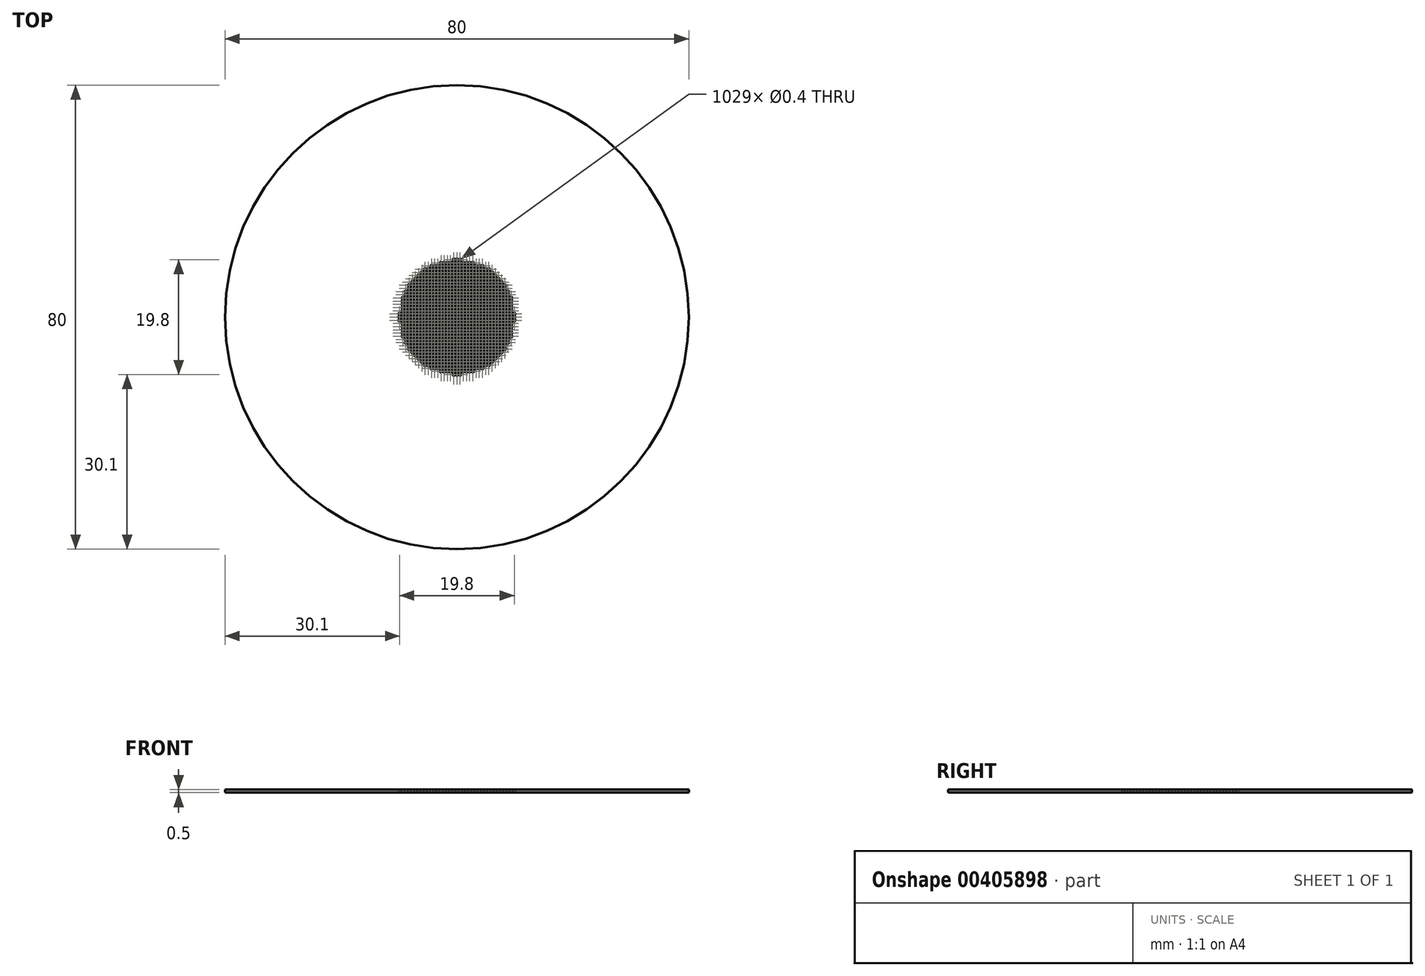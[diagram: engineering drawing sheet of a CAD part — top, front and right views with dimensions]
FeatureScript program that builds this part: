
annotation { "Feature Type Name" : "Feature", "Feature Type Description" : "" }
export const myFeature = defineFeature(function(context is Context, id is Id, definition is map)
    precondition{}
    {
        {
            var Q0;
            Q0=qCreatedBy(makeId("Top.planeOp"),FACE);
            var sketch = newSketch(context, id + "F0", { "sketchPlane" : qUnion([Q0])});
            skCircle(sketch, "E0", {"center": v(0, 0) * mm, "radius": 0.2 * mm});
            skCircle(sketch, "E1.0.1.0", {"center": v(0, 0.55) * mm, "radius": 0.2 * mm});
            skCircle(sketch, "E1.0.2.0", {"center": v(0, 1.1) * mm, "radius": 0.2 * mm});
            skCircle(sketch, "E1.0.3.0", {"center": v(0, 1.65) * mm, "radius": 0.2 * mm});
            skCircle(sketch, "E1.0.4.0", {"center": v(0, 2.2) * mm, "radius": 0.2 * mm});
            skCircle(sketch, "E1.0.5.0", {"center": v(0, 2.75) * mm, "radius": 0.2 * mm});
            skCircle(sketch, "E1.0.6.0", {"center": v(0, 3.3) * mm, "radius": 0.2 * mm});
            skCircle(sketch, "E1.0.7.0", {"center": v(0, 3.85) * mm, "radius": 0.2 * mm});
            skCircle(sketch, "E1.0.8.0", {"center": v(0, 4.4) * mm, "radius": 0.2 * mm});
            skCircle(sketch, "E1.0.9.0", {"center": v(0, 4.95) * mm, "radius": 0.2 * mm});
            skCircle(sketch, "E1.0.10.0", {"center": v(0, 5.5) * mm, "radius": 0.2 * mm});
            skCircle(sketch, "E1.0.11.0", {"center": v(0, 6.05) * mm, "radius": 0.2 * mm});
            skCircle(sketch, "E1.0.12.0", {"center": v(0, 6.6) * mm, "radius": 0.2 * mm});
            skCircle(sketch, "E1.0.13.0", {"center": v(0, 7.15) * mm, "radius": 0.2 * mm});
            skCircle(sketch, "E1.0.14.0", {"center": v(0, 7.7) * mm, "radius": 0.2 * mm});
            skCircle(sketch, "E1.0.15.0", {"center": v(0, 8.25) * mm, "radius": 0.2 * mm});
            skCircle(sketch, "E1.0.16.0", {"center": v(0, 8.8) * mm, "radius": 0.2 * mm});
            skCircle(sketch, "E1.0.17.0", {"center": v(0, 9.35) * mm, "radius": 0.2 * mm});
            skCircle(sketch, "E1.0.18.0", {"center": v(0, 9.9) * mm, "radius": 0.2 * mm});
            skCircle(sketch, "E1.1.0.0", {"center": v(0.55, 0) * mm, "radius": 0.2 * mm});
            skCircle(sketch, "E1.1.1.0", {"center": v(0.55, 0.55) * mm, "radius": 0.2 * mm});
            skCircle(sketch, "E1.1.2.0", {"center": v(0.55, 1.1) * mm, "radius": 0.2 * mm});
            skCircle(sketch, "E1.1.3.0", {"center": v(0.55, 1.65) * mm, "radius": 0.2 * mm});
            skCircle(sketch, "E1.1.4.0", {"center": v(0.55, 2.2) * mm, "radius": 0.2 * mm});
            skCircle(sketch, "E1.1.5.0", {"center": v(0.55, 2.75) * mm, "radius": 0.2 * mm});
            skCircle(sketch, "E1.1.6.0", {"center": v(0.55, 3.3) * mm, "radius": 0.2 * mm});
            skCircle(sketch, "E1.1.7.0", {"center": v(0.55, 3.85) * mm, "radius": 0.2 * mm});
            skCircle(sketch, "E1.1.8.0", {"center": v(0.55, 4.4) * mm, "radius": 0.2 * mm});
            skCircle(sketch, "E1.1.9.0", {"center": v(0.55, 4.95) * mm, "radius": 0.2 * mm});
            skCircle(sketch, "E1.1.10.0", {"center": v(0.55, 5.5) * mm, "radius": 0.2 * mm});
            skCircle(sketch, "E1.1.11.0", {"center": v(0.55, 6.05) * mm, "radius": 0.2 * mm});
            skCircle(sketch, "E1.1.12.0", {"center": v(0.55, 6.6) * mm, "radius": 0.2 * mm});
            skCircle(sketch, "E1.1.13.0", {"center": v(0.55, 7.15) * mm, "radius": 0.2 * mm});
            skCircle(sketch, "E1.1.14.0", {"center": v(0.55, 7.7) * mm, "radius": 0.2 * mm});
            skCircle(sketch, "E1.1.15.0", {"center": v(0.55, 8.25) * mm, "radius": 0.2 * mm});
            skCircle(sketch, "E1.1.16.0", {"center": v(0.55, 8.8) * mm, "radius": 0.2 * mm});
            skCircle(sketch, "E1.1.17.0", {"center": v(0.55, 9.35) * mm, "radius": 0.2 * mm});
            skCircle(sketch, "E1.1.18.0", {"center": v(0.55, 9.9) * mm, "radius": 0.2 * mm});
            skCircle(sketch, "E1.2.0.0", {"center": v(1.1, 0) * mm, "radius": 0.2 * mm});
            skCircle(sketch, "E1.2.1.0", {"center": v(1.1, 0.55) * mm, "radius": 0.2 * mm});
            skCircle(sketch, "E1.2.2.0", {"center": v(1.1, 1.1) * mm, "radius": 0.2 * mm});
            skCircle(sketch, "E1.2.3.0", {"center": v(1.1, 1.65) * mm, "radius": 0.2 * mm});
            skCircle(sketch, "E1.2.4.0", {"center": v(1.1, 2.2) * mm, "radius": 0.2 * mm});
            skCircle(sketch, "E1.2.5.0", {"center": v(1.1, 2.75) * mm, "radius": 0.2 * mm});
            skCircle(sketch, "E1.2.6.0", {"center": v(1.1, 3.3) * mm, "radius": 0.2 * mm});
            skCircle(sketch, "E1.2.7.0", {"center": v(1.1, 3.85) * mm, "radius": 0.2 * mm});
            skCircle(sketch, "E1.2.8.0", {"center": v(1.1, 4.4) * mm, "radius": 0.2 * mm});
            skCircle(sketch, "E1.2.9.0", {"center": v(1.1, 4.95) * mm, "radius": 0.2 * mm});
            skCircle(sketch, "E1.2.10.0", {"center": v(1.1, 5.5) * mm, "radius": 0.2 * mm});
            skCircle(sketch, "E1.2.11.0", {"center": v(1.1, 6.05) * mm, "radius": 0.2 * mm});
            skCircle(sketch, "E1.2.12.0", {"center": v(1.1, 6.6) * mm, "radius": 0.2 * mm});
            skCircle(sketch, "E1.2.13.0", {"center": v(1.1, 7.15) * mm, "radius": 0.2 * mm});
            skCircle(sketch, "E1.2.14.0", {"center": v(1.1, 7.7) * mm, "radius": 0.2 * mm});
            skCircle(sketch, "E1.2.15.0", {"center": v(1.1, 8.25) * mm, "radius": 0.2 * mm});
            skCircle(sketch, "E1.2.16.0", {"center": v(1.1, 8.8) * mm, "radius": 0.2 * mm});
            skCircle(sketch, "E1.2.17.0", {"center": v(1.1, 9.35) * mm, "radius": 0.2 * mm});
            skCircle(sketch, "E1.3.0.0", {"center": v(1.65, 0) * mm, "radius": 0.2 * mm});
            skCircle(sketch, "E1.3.1.0", {"center": v(1.65, 0.55) * mm, "radius": 0.2 * mm});
            skCircle(sketch, "E1.3.2.0", {"center": v(1.65, 1.1) * mm, "radius": 0.2 * mm});
            skCircle(sketch, "E1.3.3.0", {"center": v(1.65, 1.65) * mm, "radius": 0.2 * mm});
            skCircle(sketch, "E1.3.4.0", {"center": v(1.65, 2.2) * mm, "radius": 0.2 * mm});
            skCircle(sketch, "E1.3.5.0", {"center": v(1.65, 2.75) * mm, "radius": 0.2 * mm});
            skCircle(sketch, "E1.3.6.0", {"center": v(1.65, 3.3) * mm, "radius": 0.2 * mm});
            skCircle(sketch, "E1.3.7.0", {"center": v(1.65, 3.85) * mm, "radius": 0.2 * mm});
            skCircle(sketch, "E1.3.8.0", {"center": v(1.65, 4.4) * mm, "radius": 0.2 * mm});
            skCircle(sketch, "E1.3.9.0", {"center": v(1.65, 4.95) * mm, "radius": 0.2 * mm});
            skCircle(sketch, "E1.3.10.0", {"center": v(1.65, 5.5) * mm, "radius": 0.2 * mm});
            skCircle(sketch, "E1.3.11.0", {"center": v(1.65, 6.05) * mm, "radius": 0.2 * mm});
            skCircle(sketch, "E1.3.12.0", {"center": v(1.65, 6.6) * mm, "radius": 0.2 * mm});
            skCircle(sketch, "E1.3.13.0", {"center": v(1.65, 7.15) * mm, "radius": 0.2 * mm});
            skCircle(sketch, "E1.3.14.0", {"center": v(1.65, 7.7) * mm, "radius": 0.2 * mm});
            skCircle(sketch, "E1.3.15.0", {"center": v(1.65, 8.25) * mm, "radius": 0.2 * mm});
            skCircle(sketch, "E1.3.16.0", {"center": v(1.65, 8.8) * mm, "radius": 0.2 * mm});
            skCircle(sketch, "E1.3.17.0", {"center": v(1.65, 9.35) * mm, "radius": 0.2 * mm});
            skCircle(sketch, "E1.4.0.0", {"center": v(2.2, 0) * mm, "radius": 0.2 * mm});
            skCircle(sketch, "E1.4.1.0", {"center": v(2.2, 0.55) * mm, "radius": 0.2 * mm});
            skCircle(sketch, "E1.4.2.0", {"center": v(2.2, 1.1) * mm, "radius": 0.2 * mm});
            skCircle(sketch, "E1.4.3.0", {"center": v(2.2, 1.65) * mm, "radius": 0.2 * mm});
            skCircle(sketch, "E1.4.4.0", {"center": v(2.2, 2.2) * mm, "radius": 0.2 * mm});
            skCircle(sketch, "E1.4.5.0", {"center": v(2.2, 2.75) * mm, "radius": 0.2 * mm});
            skCircle(sketch, "E1.4.6.0", {"center": v(2.2, 3.3) * mm, "radius": 0.2 * mm});
            skCircle(sketch, "E1.4.7.0", {"center": v(2.2, 3.85) * mm, "radius": 0.2 * mm});
            skCircle(sketch, "E1.4.8.0", {"center": v(2.2, 4.4) * mm, "radius": 0.2 * mm});
            skCircle(sketch, "E1.4.9.0", {"center": v(2.2, 4.95) * mm, "radius": 0.2 * mm});
            skCircle(sketch, "E1.4.10.0", {"center": v(2.2, 5.5) * mm, "radius": 0.2 * mm});
            skCircle(sketch, "E1.4.11.0", {"center": v(2.2, 6.05) * mm, "radius": 0.2 * mm});
            skCircle(sketch, "E1.4.12.0", {"center": v(2.2, 6.6) * mm, "radius": 0.2 * mm});
            skCircle(sketch, "E1.4.13.0", {"center": v(2.2, 7.15) * mm, "radius": 0.2 * mm});
            skCircle(sketch, "E1.4.14.0", {"center": v(2.2, 7.7) * mm, "radius": 0.2 * mm});
            skCircle(sketch, "E1.4.15.0", {"center": v(2.2, 8.25) * mm, "radius": 0.2 * mm});
            skCircle(sketch, "E1.4.16.0", {"center": v(2.2, 8.8) * mm, "radius": 0.2 * mm});
            skCircle(sketch, "E1.4.17.0", {"center": v(2.2, 9.35) * mm, "radius": 0.2 * mm});
            skCircle(sketch, "E1.5.0.0", {"center": v(2.75, 0) * mm, "radius": 0.2 * mm});
            skCircle(sketch, "E1.5.1.0", {"center": v(2.75, 0.55) * mm, "radius": 0.2 * mm});
            skCircle(sketch, "E1.5.2.0", {"center": v(2.75, 1.1) * mm, "radius": 0.2 * mm});
            skCircle(sketch, "E1.5.3.0", {"center": v(2.75, 1.65) * mm, "radius": 0.2 * mm});
            skCircle(sketch, "E1.5.4.0", {"center": v(2.75, 2.2) * mm, "radius": 0.2 * mm});
            skCircle(sketch, "E1.5.5.0", {"center": v(2.75, 2.75) * mm, "radius": 0.2 * mm});
            skCircle(sketch, "E1.5.6.0", {"center": v(2.75, 3.3) * mm, "radius": 0.2 * mm});
            skCircle(sketch, "E1.5.7.0", {"center": v(2.75, 3.85) * mm, "radius": 0.2 * mm});
            skCircle(sketch, "E1.5.8.0", {"center": v(2.75, 4.4) * mm, "radius": 0.2 * mm});
            skCircle(sketch, "E1.5.9.0", {"center": v(2.75, 4.95) * mm, "radius": 0.2 * mm});
            skCircle(sketch, "E1.5.10.0", {"center": v(2.75, 5.5) * mm, "radius": 0.2 * mm});
            skCircle(sketch, "E1.5.11.0", {"center": v(2.75, 6.05) * mm, "radius": 0.2 * mm});
            skCircle(sketch, "E1.5.12.0", {"center": v(2.75, 6.6) * mm, "radius": 0.2 * mm});
            skCircle(sketch, "E1.5.13.0", {"center": v(2.75, 7.15) * mm, "radius": 0.2 * mm});
            skCircle(sketch, "E1.5.14.0", {"center": v(2.75, 7.7) * mm, "radius": 0.2 * mm});
            skCircle(sketch, "E1.5.15.0", {"center": v(2.75, 8.25) * mm, "radius": 0.2 * mm});
            skCircle(sketch, "E1.5.16.0", {"center": v(2.75, 8.8) * mm, "radius": 0.2 * mm});
            skCircle(sketch, "E1.5.17.0", {"center": v(2.75, 9.35) * mm, "radius": 0.2 * mm});
            skCircle(sketch, "E1.6.0.0", {"center": v(3.3, 0) * mm, "radius": 0.2 * mm});
            skCircle(sketch, "E1.6.1.0", {"center": v(3.3, 0.55) * mm, "radius": 0.2 * mm});
            skCircle(sketch, "E1.6.2.0", {"center": v(3.3, 1.1) * mm, "radius": 0.2 * mm});
            skCircle(sketch, "E1.6.3.0", {"center": v(3.3, 1.65) * mm, "radius": 0.2 * mm});
            skCircle(sketch, "E1.6.4.0", {"center": v(3.3, 2.2) * mm, "radius": 0.2 * mm});
            skCircle(sketch, "E1.6.5.0", {"center": v(3.3, 2.75) * mm, "radius": 0.2 * mm});
            skCircle(sketch, "E1.6.6.0", {"center": v(3.3, 3.3) * mm, "radius": 0.2 * mm});
            skCircle(sketch, "E1.6.7.0", {"center": v(3.3, 3.85) * mm, "radius": 0.2 * mm});
            skCircle(sketch, "E1.6.8.0", {"center": v(3.3, 4.4) * mm, "radius": 0.2 * mm});
            skCircle(sketch, "E1.6.9.0", {"center": v(3.3, 4.95) * mm, "radius": 0.2 * mm});
            skCircle(sketch, "E1.6.10.0", {"center": v(3.3, 5.5) * mm, "radius": 0.2 * mm});
            skCircle(sketch, "E1.6.11.0", {"center": v(3.3, 6.05) * mm, "radius": 0.2 * mm});
            skCircle(sketch, "E1.6.12.0", {"center": v(3.3, 6.6) * mm, "radius": 0.2 * mm});
            skCircle(sketch, "E1.6.13.0", {"center": v(3.3, 7.15) * mm, "radius": 0.2 * mm});
            skCircle(sketch, "E1.6.14.0", {"center": v(3.3, 7.7) * mm, "radius": 0.2 * mm});
            skCircle(sketch, "E1.6.15.0", {"center": v(3.3, 8.25) * mm, "radius": 0.2 * mm});
            skCircle(sketch, "E1.6.16.0", {"center": v(3.3, 8.8) * mm, "radius": 0.2 * mm});
            skCircle(sketch, "E1.7.0.0", {"center": v(3.85, 0) * mm, "radius": 0.2 * mm});
            skCircle(sketch, "E1.7.1.0", {"center": v(3.85, 0.55) * mm, "radius": 0.2 * mm});
            skCircle(sketch, "E1.7.2.0", {"center": v(3.85, 1.1) * mm, "radius": 0.2 * mm});
            skCircle(sketch, "E1.7.3.0", {"center": v(3.85, 1.65) * mm, "radius": 0.2 * mm});
            skCircle(sketch, "E1.7.4.0", {"center": v(3.85, 2.2) * mm, "radius": 0.2 * mm});
            skCircle(sketch, "E1.7.5.0", {"center": v(3.85, 2.75) * mm, "radius": 0.2 * mm});
            skCircle(sketch, "E1.7.6.0", {"center": v(3.85, 3.3) * mm, "radius": 0.2 * mm});
            skCircle(sketch, "E1.7.7.0", {"center": v(3.85, 3.85) * mm, "radius": 0.2 * mm});
            skCircle(sketch, "E1.7.8.0", {"center": v(3.85, 4.4) * mm, "radius": 0.2 * mm});
            skCircle(sketch, "E1.7.9.0", {"center": v(3.85, 4.95) * mm, "radius": 0.2 * mm});
            skCircle(sketch, "E1.7.10.0", {"center": v(3.85, 5.5) * mm, "radius": 0.2 * mm});
            skCircle(sketch, "E1.7.11.0", {"center": v(3.85, 6.05) * mm, "radius": 0.2 * mm});
            skCircle(sketch, "E1.7.12.0", {"center": v(3.85, 6.6) * mm, "radius": 0.2 * mm});
            skCircle(sketch, "E1.7.13.0", {"center": v(3.85, 7.15) * mm, "radius": 0.2 * mm});
            skCircle(sketch, "E1.7.14.0", {"center": v(3.85, 7.7) * mm, "radius": 0.2 * mm});
            skCircle(sketch, "E1.7.15.0", {"center": v(3.85, 8.25) * mm, "radius": 0.2 * mm});
            skCircle(sketch, "E1.7.16.0", {"center": v(3.85, 8.8) * mm, "radius": 0.2 * mm});
            skCircle(sketch, "E1.8.0.0", {"center": v(4.4, 0) * mm, "radius": 0.2 * mm});
            skCircle(sketch, "E1.8.1.0", {"center": v(4.4, 0.55) * mm, "radius": 0.2 * mm});
            skCircle(sketch, "E1.8.2.0", {"center": v(4.4, 1.1) * mm, "radius": 0.2 * mm});
            skCircle(sketch, "E1.8.3.0", {"center": v(4.4, 1.65) * mm, "radius": 0.2 * mm});
            skCircle(sketch, "E1.8.4.0", {"center": v(4.4, 2.2) * mm, "radius": 0.2 * mm});
            skCircle(sketch, "E1.8.5.0", {"center": v(4.4, 2.75) * mm, "radius": 0.2 * mm});
            skCircle(sketch, "E1.8.6.0", {"center": v(4.4, 3.3) * mm, "radius": 0.2 * mm});
            skCircle(sketch, "E1.8.7.0", {"center": v(4.4, 3.85) * mm, "radius": 0.2 * mm});
            skCircle(sketch, "E1.8.8.0", {"center": v(4.4, 4.4) * mm, "radius": 0.2 * mm});
            skCircle(sketch, "E1.8.9.0", {"center": v(4.4, 4.95) * mm, "radius": 0.2 * mm});
            skCircle(sketch, "E1.8.10.0", {"center": v(4.4, 5.5) * mm, "radius": 0.2 * mm});
            skCircle(sketch, "E1.8.11.0", {"center": v(4.4, 6.05) * mm, "radius": 0.2 * mm});
            skCircle(sketch, "E1.8.12.0", {"center": v(4.4, 6.6) * mm, "radius": 0.2 * mm});
            skCircle(sketch, "E1.8.13.0", {"center": v(4.4, 7.15) * mm, "radius": 0.2 * mm});
            skCircle(sketch, "E1.8.14.0", {"center": v(4.4, 7.7) * mm, "radius": 0.2 * mm});
            skCircle(sketch, "E1.8.15.0", {"center": v(4.4, 8.25) * mm, "radius": 0.2 * mm});
            skCircle(sketch, "E1.8.16.0", {"center": v(4.4, 8.8) * mm, "radius": 0.2 * mm});
            skCircle(sketch, "E1.9.0.0", {"center": v(4.95, 0) * mm, "radius": 0.2 * mm});
            skCircle(sketch, "E1.9.1.0", {"center": v(4.95, 0.55) * mm, "radius": 0.2 * mm});
            skCircle(sketch, "E1.9.2.0", {"center": v(4.95, 1.1) * mm, "radius": 0.2 * mm});
            skCircle(sketch, "E1.9.3.0", {"center": v(4.95, 1.65) * mm, "radius": 0.2 * mm});
            skCircle(sketch, "E1.9.4.0", {"center": v(4.95, 2.2) * mm, "radius": 0.2 * mm});
            skCircle(sketch, "E1.9.5.0", {"center": v(4.95, 2.75) * mm, "radius": 0.2 * mm});
            skCircle(sketch, "E1.9.6.0", {"center": v(4.95, 3.3) * mm, "radius": 0.2 * mm});
            skCircle(sketch, "E1.9.7.0", {"center": v(4.95, 3.85) * mm, "radius": 0.2 * mm});
            skCircle(sketch, "E1.9.8.0", {"center": v(4.95, 4.4) * mm, "radius": 0.2 * mm});
            skCircle(sketch, "E1.9.9.0", {"center": v(4.95, 4.95) * mm, "radius": 0.2 * mm});
            skCircle(sketch, "E1.9.10.0", {"center": v(4.95, 5.5) * mm, "radius": 0.2 * mm});
            skCircle(sketch, "E1.9.11.0", {"center": v(4.95, 6.05) * mm, "radius": 0.2 * mm});
            skCircle(sketch, "E1.9.12.0", {"center": v(4.95, 6.6) * mm, "radius": 0.2 * mm});
            skCircle(sketch, "E1.9.13.0", {"center": v(4.95, 7.15) * mm, "radius": 0.2 * mm});
            skCircle(sketch, "E1.9.14.0", {"center": v(4.95, 7.7) * mm, "radius": 0.2 * mm});
            skCircle(sketch, "E1.9.15.0", {"center": v(4.95, 8.25) * mm, "radius": 0.2 * mm});
            skCircle(sketch, "E1.10.0.0", {"center": v(5.5, 0) * mm, "radius": 0.2 * mm});
            skCircle(sketch, "E1.10.1.0", {"center": v(5.5, 0.55) * mm, "radius": 0.2 * mm});
            skCircle(sketch, "E1.10.2.0", {"center": v(5.5, 1.1) * mm, "radius": 0.2 * mm});
            skCircle(sketch, "E1.10.3.0", {"center": v(5.5, 1.65) * mm, "radius": 0.2 * mm});
            skCircle(sketch, "E1.10.4.0", {"center": v(5.5, 2.2) * mm, "radius": 0.2 * mm});
            skCircle(sketch, "E1.10.5.0", {"center": v(5.5, 2.75) * mm, "radius": 0.2 * mm});
            skCircle(sketch, "E1.10.6.0", {"center": v(5.5, 3.3) * mm, "radius": 0.2 * mm});
            skCircle(sketch, "E1.10.7.0", {"center": v(5.5, 3.85) * mm, "radius": 0.2 * mm});
            skCircle(sketch, "E1.10.8.0", {"center": v(5.5, 4.4) * mm, "radius": 0.2 * mm});
            skCircle(sketch, "E1.10.9.0", {"center": v(5.5, 4.95) * mm, "radius": 0.2 * mm});
            skCircle(sketch, "E1.10.10.0", {"center": v(5.5, 5.5) * mm, "radius": 0.2 * mm});
            skCircle(sketch, "E1.10.11.0", {"center": v(5.5, 6.05) * mm, "radius": 0.2 * mm});
            skCircle(sketch, "E1.10.12.0", {"center": v(5.5, 6.6) * mm, "radius": 0.2 * mm});
            skCircle(sketch, "E1.10.13.0", {"center": v(5.5, 7.15) * mm, "radius": 0.2 * mm});
            skCircle(sketch, "E1.10.14.0", {"center": v(5.5, 7.7) * mm, "radius": 0.2 * mm});
            skCircle(sketch, "E1.10.15.0", {"center": v(5.5, 8.25) * mm, "radius": 0.2 * mm});
            skCircle(sketch, "E1.11.0.0", {"center": v(6.05, 0) * mm, "radius": 0.2 * mm});
            skCircle(sketch, "E1.11.1.0", {"center": v(6.05, 0.55) * mm, "radius": 0.2 * mm});
            skCircle(sketch, "E1.11.2.0", {"center": v(6.05, 1.1) * mm, "radius": 0.2 * mm});
            skCircle(sketch, "E1.11.3.0", {"center": v(6.05, 1.65) * mm, "radius": 0.2 * mm});
            skCircle(sketch, "E1.11.4.0", {"center": v(6.05, 2.2) * mm, "radius": 0.2 * mm});
            skCircle(sketch, "E1.11.5.0", {"center": v(6.05, 2.75) * mm, "radius": 0.2 * mm});
            skCircle(sketch, "E1.11.6.0", {"center": v(6.05, 3.3) * mm, "radius": 0.2 * mm});
            skCircle(sketch, "E1.11.7.0", {"center": v(6.05, 3.85) * mm, "radius": 0.2 * mm});
            skCircle(sketch, "E1.11.8.0", {"center": v(6.05, 4.4) * mm, "radius": 0.2 * mm});
            skCircle(sketch, "E1.11.9.0", {"center": v(6.05, 4.95) * mm, "radius": 0.2 * mm});
            skCircle(sketch, "E1.11.10.0", {"center": v(6.05, 5.5) * mm, "radius": 0.2 * mm});
            skCircle(sketch, "E1.11.11.0", {"center": v(6.05, 6.05) * mm, "radius": 0.2 * mm});
            skCircle(sketch, "E1.11.12.0", {"center": v(6.05, 6.6) * mm, "radius": 0.2 * mm});
            skCircle(sketch, "E1.11.13.0", {"center": v(6.05, 7.15) * mm, "radius": 0.2 * mm});
            skCircle(sketch, "E1.11.14.0", {"center": v(6.05, 7.7) * mm, "radius": 0.2 * mm});
            skCircle(sketch, "E1.12.0.0", {"center": v(6.6, 0) * mm, "radius": 0.2 * mm});
            skCircle(sketch, "E1.12.1.0", {"center": v(6.6, 0.55) * mm, "radius": 0.2 * mm});
            skCircle(sketch, "E1.12.2.0", {"center": v(6.6, 1.1) * mm, "radius": 0.2 * mm});
            skCircle(sketch, "E1.12.3.0", {"center": v(6.6, 1.65) * mm, "radius": 0.2 * mm});
            skCircle(sketch, "E1.12.4.0", {"center": v(6.6, 2.2) * mm, "radius": 0.2 * mm});
            skCircle(sketch, "E1.12.5.0", {"center": v(6.6, 2.75) * mm, "radius": 0.2 * mm});
            skCircle(sketch, "E1.12.6.0", {"center": v(6.6, 3.3) * mm, "radius": 0.2 * mm});
            skCircle(sketch, "E1.12.7.0", {"center": v(6.6, 3.85) * mm, "radius": 0.2 * mm});
            skCircle(sketch, "E1.12.8.0", {"center": v(6.6, 4.4) * mm, "radius": 0.2 * mm});
            skCircle(sketch, "E1.12.9.0", {"center": v(6.6, 4.95) * mm, "radius": 0.2 * mm});
            skCircle(sketch, "E1.12.10.0", {"center": v(6.6, 5.5) * mm, "radius": 0.2 * mm});
            skCircle(sketch, "E1.12.11.0", {"center": v(6.6, 6.05) * mm, "radius": 0.2 * mm});
            skCircle(sketch, "E1.12.12.0", {"center": v(6.6, 6.6) * mm, "radius": 0.2 * mm});
            skCircle(sketch, "E1.12.13.0", {"center": v(6.6, 7.15) * mm, "radius": 0.2 * mm});
            skCircle(sketch, "E1.13.0.0", {"center": v(7.15, 0) * mm, "radius": 0.2 * mm});
            skCircle(sketch, "E1.13.1.0", {"center": v(7.15, 0.55) * mm, "radius": 0.2 * mm});
            skCircle(sketch, "E1.13.2.0", {"center": v(7.15, 1.1) * mm, "radius": 0.2 * mm});
            skCircle(sketch, "E1.13.3.0", {"center": v(7.15, 1.65) * mm, "radius": 0.2 * mm});
            skCircle(sketch, "E1.13.4.0", {"center": v(7.15, 2.2) * mm, "radius": 0.2 * mm});
            skCircle(sketch, "E1.13.5.0", {"center": v(7.15, 2.75) * mm, "radius": 0.2 * mm});
            skCircle(sketch, "E1.13.6.0", {"center": v(7.15, 3.3) * mm, "radius": 0.2 * mm});
            skCircle(sketch, "E1.13.7.0", {"center": v(7.15, 3.85) * mm, "radius": 0.2 * mm});
            skCircle(sketch, "E1.13.8.0", {"center": v(7.15, 4.4) * mm, "radius": 0.2 * mm});
            skCircle(sketch, "E1.13.9.0", {"center": v(7.15, 4.95) * mm, "radius": 0.2 * mm});
            skCircle(sketch, "E1.13.10.0", {"center": v(7.15, 5.5) * mm, "radius": 0.2 * mm});
            skCircle(sketch, "E1.13.11.0", {"center": v(7.15, 6.05) * mm, "radius": 0.2 * mm});
            skCircle(sketch, "E1.13.12.0", {"center": v(7.15, 6.6) * mm, "radius": 0.2 * mm});
            skCircle(sketch, "E1.14.0.0", {"center": v(7.7, 0) * mm, "radius": 0.2 * mm});
            skCircle(sketch, "E1.14.1.0", {"center": v(7.7, 0.55) * mm, "radius": 0.2 * mm});
            skCircle(sketch, "E1.14.2.0", {"center": v(7.7, 1.1) * mm, "radius": 0.2 * mm});
            skCircle(sketch, "E1.14.3.0", {"center": v(7.7, 1.65) * mm, "radius": 0.2 * mm});
            skCircle(sketch, "E1.14.4.0", {"center": v(7.7, 2.2) * mm, "radius": 0.2 * mm});
            skCircle(sketch, "E1.14.5.0", {"center": v(7.7, 2.75) * mm, "radius": 0.2 * mm});
            skCircle(sketch, "E1.14.6.0", {"center": v(7.7, 3.3) * mm, "radius": 0.2 * mm});
            skCircle(sketch, "E1.14.7.0", {"center": v(7.7, 3.85) * mm, "radius": 0.2 * mm});
            skCircle(sketch, "E1.14.8.0", {"center": v(7.7, 4.4) * mm, "radius": 0.2 * mm});
            skCircle(sketch, "E1.14.9.0", {"center": v(7.7, 4.95) * mm, "radius": 0.2 * mm});
            skCircle(sketch, "E1.14.10.0", {"center": v(7.7, 5.5) * mm, "radius": 0.2 * mm});
            skCircle(sketch, "E1.14.11.0", {"center": v(7.7, 6.05) * mm, "radius": 0.2 * mm});
            skCircle(sketch, "E1.15.0.0", {"center": v(8.25, 0) * mm, "radius": 0.2 * mm});
            skCircle(sketch, "E1.15.1.0", {"center": v(8.25, 0.55) * mm, "radius": 0.2 * mm});
            skCircle(sketch, "E1.15.2.0", {"center": v(8.25, 1.1) * mm, "radius": 0.2 * mm});
            skCircle(sketch, "E1.15.3.0", {"center": v(8.25, 1.65) * mm, "radius": 0.2 * mm});
            skCircle(sketch, "E1.15.4.0", {"center": v(8.25, 2.2) * mm, "radius": 0.2 * mm});
            skCircle(sketch, "E1.15.5.0", {"center": v(8.25, 2.75) * mm, "radius": 0.2 * mm});
            skCircle(sketch, "E1.15.6.0", {"center": v(8.25, 3.3) * mm, "radius": 0.2 * mm});
            skCircle(sketch, "E1.15.7.0", {"center": v(8.25, 3.85) * mm, "radius": 0.2 * mm});
            skCircle(sketch, "E1.15.8.0", {"center": v(8.25, 4.4) * mm, "radius": 0.2 * mm});
            skCircle(sketch, "E1.15.9.0", {"center": v(8.25, 4.95) * mm, "radius": 0.2 * mm});
            skCircle(sketch, "E1.15.10.0", {"center": v(8.25, 5.5) * mm, "radius": 0.2 * mm});
            skCircle(sketch, "E1.16.0.0", {"center": v(8.8, 0) * mm, "radius": 0.2 * mm});
            skCircle(sketch, "E1.16.1.0", {"center": v(8.8, 0.55) * mm, "radius": 0.2 * mm});
            skCircle(sketch, "E1.16.2.0", {"center": v(8.8, 1.1) * mm, "radius": 0.2 * mm});
            skCircle(sketch, "E1.16.3.0", {"center": v(8.8, 1.65) * mm, "radius": 0.2 * mm});
            skCircle(sketch, "E1.16.4.0", {"center": v(8.8, 2.2) * mm, "radius": 0.2 * mm});
            skCircle(sketch, "E1.16.5.0", {"center": v(8.8, 2.75) * mm, "radius": 0.2 * mm});
            skCircle(sketch, "E1.16.6.0", {"center": v(8.8, 3.3) * mm, "radius": 0.2 * mm});
            skCircle(sketch, "E1.16.7.0", {"center": v(8.8, 3.85) * mm, "radius": 0.2 * mm});
            skCircle(sketch, "E1.16.8.0", {"center": v(8.8, 4.4) * mm, "radius": 0.2 * mm});
            skCircle(sketch, "E1.17.0.0", {"center": v(9.35, 0) * mm, "radius": 0.2 * mm});
            skCircle(sketch, "E1.17.1.0", {"center": v(9.35, 0.55) * mm, "radius": 0.2 * mm});
            skCircle(sketch, "E1.17.2.0", {"center": v(9.35, 1.1) * mm, "radius": 0.2 * mm});
            skCircle(sketch, "E1.17.3.0", {"center": v(9.35, 1.65) * mm, "radius": 0.2 * mm});
            skCircle(sketch, "E1.17.4.0", {"center": v(9.35, 2.2) * mm, "radius": 0.2 * mm});
            skCircle(sketch, "E1.17.5.0", {"center": v(9.35, 2.75) * mm, "radius": 0.2 * mm});
            skCircle(sketch, "E1.17.6.0", {"center": v(9.35, 3.3) * mm, "radius": 0.2 * mm});
            skCircle(sketch, "E1.18.0.0", {"center": v(9.9, 0) * mm, "radius": 0.2 * mm});
            skCircle(sketch, "E1.18.1.0", {"center": v(9.9, 0.55) * mm, "radius": 0.2 * mm});
            skLineSegment(sketch, "E1.direction1", {"start": v(0, 0) * mm, "end": v(0.55, 0) * mm, "construction": true});
            skLineSegment(sketch, "E1.direction2", {"start": v(0, 0) * mm, "end": v(0, 0.55) * mm, "construction": true});
            skCircle(sketch, "E2.MirrorC", {"center": v(3.3, -1.1) * mm, "radius": 0.2 * mm});
            skCircle(sketch, "E3.MirrorC", {"center": v(2.75, -2.2) * mm, "radius": 0.2 * mm});
            skCircle(sketch, "E4.MirrorC", {"center": v(5.5, -8.25) * mm, "radius": 0.2 * mm});
            skCircle(sketch, "E5.MirrorC", {"center": v(4.95, -8.25) * mm, "radius": 0.2 * mm});
            skCircle(sketch, "E6.MirrorC", {"center": v(4.4, -8.8) * mm, "radius": 0.2 * mm});
            skCircle(sketch, "E7.MirrorC", {"center": v(9.35, -2.75) * mm, "radius": 0.2 * mm});
            skCircle(sketch, "E8.MirrorC", {"center": v(8.25, -4.95) * mm, "radius": 0.2 * mm});
            skCircle(sketch, "E9.MirrorC", {"center": v(7.15, -1.1) * mm, "radius": 0.2 * mm});
            skCircle(sketch, "E10.MirrorC", {"center": v(7.7, -2.75) * mm, "radius": 0.2 * mm});
            skCircle(sketch, "E11.MirrorC", {"center": v(4.4, -2.75) * mm, "radius": 0.2 * mm});
            skCircle(sketch, "E12.MirrorC", {"center": v(2.2, -3.3) * mm, "radius": 0.2 * mm});
            skCircle(sketch, "E13.MirrorC", {"center": v(1.65, -4.4) * mm, "radius": 0.2 * mm});
            skCircle(sketch, "E14.MirrorC", {"center": v(1.1, -5.5) * mm, "radius": 0.2 * mm});
            skCircle(sketch, "E15.MirrorC", {"center": v(2.2, -2.75) * mm, "radius": 0.2 * mm});
            skCircle(sketch, "E16.MirrorC", {"center": v(1.65, -3.85) * mm, "radius": 0.2 * mm});
            skCircle(sketch, "E17.MirrorC", {"center": v(1.1, -4.95) * mm, "radius": 0.2 * mm});
            skCircle(sketch, "E18.MirrorC", {"center": v(3.85, -8.8) * mm, "radius": 0.2 * mm});
            skCircle(sketch, "E19.MirrorC", {"center": v(2.75, -1.65) * mm, "radius": 0.2 * mm});
            skCircle(sketch, "E20.MirrorC", {"center": v(6.05, -7.7) * mm, "radius": 0.2 * mm});
            skCircle(sketch, "E21.MirrorC", {"center": v(5.5, -7.7) * mm, "radius": 0.2 * mm});
            skCircle(sketch, "E22.MirrorC", {"center": v(4.95, -7.7) * mm, "radius": 0.2 * mm});
            skCircle(sketch, "E23.MirrorC", {"center": v(4.4, -8.25) * mm, "radius": 0.2 * mm});
            skCircle(sketch, "E24.MirrorC", {"center": v(9.35, -2.2) * mm, "radius": 0.2 * mm});
            skCircle(sketch, "E25.MirrorC", {"center": v(8.25, -4.4) * mm, "radius": 0.2 * mm});
            skCircle(sketch, "E26.MirrorC", {"center": v(3.3, -3.85) * mm, "radius": 0.2 * mm});
            skCircle(sketch, "E27.MirrorC", {"center": v(7.7, -2.2) * mm, "radius": 0.2 * mm});
            skCircle(sketch, "E28.MirrorC", {"center": v(3.85, -3.3) * mm, "radius": 0.2 * mm});
            skCircle(sketch, "E29.MirrorC", {"center": v(2.75, -4.95) * mm, "radius": 0.2 * mm});
            skCircle(sketch, "E30.MirrorC", {"center": v(6.6, -2.75) * mm, "radius": 0.2 * mm});
            skCircle(sketch, "E31.MirrorC", {"center": v(5.5, -2.2) * mm, "radius": 0.2 * mm});
            skCircle(sketch, "E32.MirrorC", {"center": v(6.05, -2.2) * mm, "radius": 0.2 * mm});
            skCircle(sketch, "E33.MirrorC", {"center": v(4.95, -2.2) * mm, "radius": 0.2 * mm});
            skCircle(sketch, "E34.MirrorC", {"center": v(8.8, -1.65) * mm, "radius": 0.2 * mm});
            skCircle(sketch, "E35.MirrorC", {"center": v(7.7, -5.5) * mm, "radius": 0.2 * mm});
            skCircle(sketch, "E36.MirrorC", {"center": v(7.15, -3.85) * mm, "radius": 0.2 * mm});
            skCircle(sketch, "E37.MirrorC", {"center": v(8.25, -5.5) * mm, "radius": 0.2 * mm});
            skCircle(sketch, "E38.MirrorC", {"center": v(9.35, -3.3) * mm, "radius": 0.2 * mm});
            skCircle(sketch, "E39.MirrorC", {"center": v(7.7, -3.3) * mm, "radius": 0.2 * mm});
            skCircle(sketch, "E40.MirrorC", {"center": v(7.15, -1.65) * mm, "radius": 0.2 * mm});
            skCircle(sketch, "E41.MirrorC", {"center": v(1.65, -4.95) * mm, "radius": 0.2 * mm});
            skCircle(sketch, "E42.MirrorC", {"center": v(2.2, -3.85) * mm, "radius": 0.2 * mm});
            skCircle(sketch, "E43.MirrorC", {"center": v(1.1, -6.05) * mm, "radius": 0.2 * mm});
            skCircle(sketch, "E44.MirrorC", {"center": v(3.85, -1.1) * mm, "radius": 0.2 * mm});
            skCircle(sketch, "E45.MirrorC", {"center": v(2.75, -2.75) * mm, "radius": 0.2 * mm});
            skCircle(sketch, "E46.MirrorC", {"center": v(3.3, -1.65) * mm, "radius": 0.2 * mm});
            skCircle(sketch, "E47.MirrorC", {"center": v(1.65, -7.7) * mm, "radius": 0.2 * mm});
            skCircle(sketch, "E48.MirrorC", {"center": v(2.2, -6.6) * mm, "radius": 0.2 * mm});
            skCircle(sketch, "E49.MirrorC", {"center": v(4.4, -3.3) * mm, "radius": 0.2 * mm});
            skCircle(sketch, "E50.MirrorC", {"center": v(1.1, -8.8) * mm, "radius": 0.2 * mm});
            skCircle(sketch, "E51.MirrorC", {"center": v(3.85, -3.85) * mm, "radius": 0.2 * mm});
            skCircle(sketch, "E52.MirrorC", {"center": v(3.3, -4.4) * mm, "radius": 0.2 * mm});
            skCircle(sketch, "E53.MirrorC", {"center": v(2.75, -5.5) * mm, "radius": 0.2 * mm});
            skCircle(sketch, "E54.MirrorC", {"center": v(6.6, -3.3) * mm, "radius": 0.2 * mm});
            skCircle(sketch, "E55.MirrorC", {"center": v(6.05, -2.75) * mm, "radius": 0.2 * mm});
            skCircle(sketch, "E56.MirrorC", {"center": v(5.5, -2.75) * mm, "radius": 0.2 * mm});
            skCircle(sketch, "E57.MirrorC", {"center": v(4.95, -2.75) * mm, "radius": 0.2 * mm});
            skCircle(sketch, "E58.MirrorC", {"center": v(8.8, -2.2) * mm, "radius": 0.2 * mm});
            skCircle(sketch, "E59.MirrorC", {"center": v(7.7, -6.05) * mm, "radius": 0.2 * mm});
            skCircle(sketch, "E60.MirrorC", {"center": v(7.15, -4.4) * mm, "radius": 0.2 * mm});
            skCircle(sketch, "E61.MirrorC", {"center": v(1.1, -9.35) * mm, "radius": 0.2 * mm});
            skCircle(sketch, "E62.MirrorC", {"center": v(3.3, -4.95) * mm, "radius": 0.2 * mm});
            skCircle(sketch, "E63.MirrorC", {"center": v(2.75, -6.05) * mm, "radius": 0.2 * mm});
            skCircle(sketch, "E64.MirrorC", {"center": v(2.2, -7.15) * mm, "radius": 0.2 * mm});
            skCircle(sketch, "E65.MirrorC", {"center": v(1.65, -8.25) * mm, "radius": 0.2 * mm});
            skCircle(sketch, "E66.MirrorC", {"center": v(5.5, -3.3) * mm, "radius": 0.2 * mm});
            skCircle(sketch, "E67.MirrorC", {"center": v(3.85, -4.4) * mm, "radius": 0.2 * mm});
            skCircle(sketch, "E68.MirrorC", {"center": v(4.95, -3.3) * mm, "radius": 0.2 * mm});
            skCircle(sketch, "E69.MirrorC", {"center": v(7.15, -4.95) * mm, "radius": 0.2 * mm});
            skCircle(sketch, "E70.MirrorC", {"center": v(4.4, -3.85) * mm, "radius": 0.2 * mm});
            skCircle(sketch, "E71.MirrorC", {"center": v(6.05, -3.3) * mm, "radius": 0.2 * mm});
            skCircle(sketch, "E72.MirrorC", {"center": v(6.6, -3.85) * mm, "radius": 0.2 * mm});
            skCircle(sketch, "E73.MirrorC", {"center": v(8.8, -2.75) * mm, "radius": 0.2 * mm});
            skCircle(sketch, "E74.MirrorC", {"center": v(1.1, -1.1) * mm, "radius": 0.2 * mm});
            skCircle(sketch, "E75.MirrorC", {"center": v(3.3, -5.5) * mm, "radius": 0.2 * mm});
            skCircle(sketch, "E76.MirrorC", {"center": v(2.75, -6.6) * mm, "radius": 0.2 * mm});
            skCircle(sketch, "E77.MirrorC", {"center": v(2.2, -7.7) * mm, "radius": 0.2 * mm});
            skCircle(sketch, "E78.MirrorC", {"center": v(1.65, -8.8) * mm, "radius": 0.2 * mm});
            skCircle(sketch, "E79.MirrorC", {"center": v(5.5, -3.85) * mm, "radius": 0.2 * mm});
            skCircle(sketch, "E80.MirrorC", {"center": v(4.95, -3.85) * mm, "radius": 0.2 * mm});
            skCircle(sketch, "E81.MirrorC", {"center": v(4.4, -4.4) * mm, "radius": 0.2 * mm});
            skCircle(sketch, "E82.MirrorC", {"center": v(3.85, -4.95) * mm, "radius": 0.2 * mm});
            skCircle(sketch, "E83.MirrorC", {"center": v(6.05, -4.4) * mm, "radius": 0.2 * mm});
            skCircle(sketch, "E84.MirrorC", {"center": v(6.6, -4.95) * mm, "radius": 0.2 * mm});
            skCircle(sketch, "E85.MirrorC", {"center": v(7.15, -6.05) * mm, "radius": 0.2 * mm});
            skCircle(sketch, "E86.MirrorC", {"center": v(8.25, -1.1) * mm, "radius": 0.2 * mm});
            skCircle(sketch, "E87.MirrorC", {"center": v(3.85, -5.5) * mm, "radius": 0.2 * mm});
            skCircle(sketch, "E88.MirrorC", {"center": v(4.4, -4.95) * mm, "radius": 0.2 * mm});
            skCircle(sketch, "E89.MirrorC", {"center": v(5.5, -4.4) * mm, "radius": 0.2 * mm});
            skCircle(sketch, "E90.MirrorC", {"center": v(4.95, -4.4) * mm, "radius": 0.2 * mm});
            skCircle(sketch, "E91.MirrorC", {"center": v(1.65, -9.35) * mm, "radius": 0.2 * mm});
            skCircle(sketch, "E92.MirrorC", {"center": v(2.2, -8.25) * mm, "radius": 0.2 * mm});
            skCircle(sketch, "E93.MirrorC", {"center": v(3.3, -6.05) * mm, "radius": 0.2 * mm});
            skCircle(sketch, "E94.MirrorC", {"center": v(2.75, -7.15) * mm, "radius": 0.2 * mm});
            skCircle(sketch, "E95.MirrorC", {"center": v(1.1, -8.25) * mm, "radius": 0.2 * mm});
            skCircle(sketch, "E96.MirrorC", {"center": v(1.65, -7.15) * mm, "radius": 0.2 * mm});
            skCircle(sketch, "E97.MirrorC", {"center": v(2.2, -6.05) * mm, "radius": 0.2 * mm});
            skCircle(sketch, "E98.MirrorC", {"center": v(7.7, -4.95) * mm, "radius": 0.2 * mm});
            skCircle(sketch, "E99.MirrorC", {"center": v(7.15, -3.3) * mm, "radius": 0.2 * mm});
            skCircle(sketch, "E100.MirrorC", {"center": v(8.8, -1.1) * mm, "radius": 0.2 * mm});
            skCircle(sketch, "E101.MirrorC", {"center": v(4.95, -1.65) * mm, "radius": 0.2 * mm});
            skCircle(sketch, "E102.MirrorC", {"center": v(5.5, -1.65) * mm, "radius": 0.2 * mm});
            skCircle(sketch, "E103.MirrorC", {"center": v(6.05, -1.65) * mm, "radius": 0.2 * mm});
            skCircle(sketch, "E104.MirrorC", {"center": v(6.6, -2.2) * mm, "radius": 0.2 * mm});
            skCircle(sketch, "E105.MirrorC", {"center": v(2.75, -4.4) * mm, "radius": 0.2 * mm});
            skCircle(sketch, "E106.MirrorC", {"center": v(3.85, -2.75) * mm, "radius": 0.2 * mm});
            skCircle(sketch, "E107.MirrorC", {"center": v(3.3, -3.3) * mm, "radius": 0.2 * mm});
            skCircle(sketch, "E108.MirrorC", {"center": v(4.4, -2.2) * mm, "radius": 0.2 * mm});
            skCircle(sketch, "E109.MirrorC", {"center": v(1.1, -7.7) * mm, "radius": 0.2 * mm});
            skCircle(sketch, "E110.MirrorC", {"center": v(1.65, -6.6) * mm, "radius": 0.2 * mm});
            skCircle(sketch, "E111.MirrorC", {"center": v(2.2, -5.5) * mm, "radius": 0.2 * mm});
            skCircle(sketch, "E112.MirrorC", {"center": v(1.65, -2.2) * mm, "radius": 0.2 * mm});
            skCircle(sketch, "E113.MirrorC", {"center": v(6.6, -5.5) * mm, "radius": 0.2 * mm});
            skCircle(sketch, "E114.MirrorC", {"center": v(8.8, -4.4) * mm, "radius": 0.2 * mm});
            skCircle(sketch, "E115.MirrorC", {"center": v(6.05, -4.95) * mm, "radius": 0.2 * mm});
            skCircle(sketch, "E116.MirrorC", {"center": v(1.1, -3.3) * mm, "radius": 0.2 * mm});
            skCircle(sketch, "E117.MirrorC", {"center": v(3.3, -7.7) * mm, "radius": 0.2 * mm});
            skCircle(sketch, "E118.MirrorC", {"center": v(2.75, -8.8) * mm, "radius": 0.2 * mm});
            skCircle(sketch, "E119.MirrorC", {"center": v(2.2, -1.1) * mm, "radius": 0.2 * mm});
            skCircle(sketch, "E120.MirrorC", {"center": v(5.5, -6.05) * mm, "radius": 0.2 * mm});
            skCircle(sketch, "E121.MirrorC", {"center": v(4.95, -6.05) * mm, "radius": 0.2 * mm});
            skCircle(sketch, "E122.MirrorC", {"center": v(4.4, -6.6) * mm, "radius": 0.2 * mm});
            skCircle(sketch, "E123.MirrorC", {"center": v(3.85, -7.15) * mm, "radius": 0.2 * mm});
            skCircle(sketch, "E124.MirrorC", {"center": v(8.25, -2.75) * mm, "radius": 0.2 * mm});
            skCircle(sketch, "E125.MirrorC", {"center": v(6.6, -6.6) * mm, "radius": 0.2 * mm});
            skCircle(sketch, "E126.MirrorC", {"center": v(6.05, -6.05) * mm, "radius": 0.2 * mm});
            skCircle(sketch, "E127.MirrorC", {"center": v(1.65, -1.65) * mm, "radius": 0.2 * mm});
            skCircle(sketch, "E128.MirrorC", {"center": v(1.1, -2.75) * mm, "radius": 0.2 * mm});
            skCircle(sketch, "E129.MirrorC", {"center": v(2.75, -8.25) * mm, "radius": 0.2 * mm});
            skCircle(sketch, "E130.MirrorC", {"center": v(3.3, -7.15) * mm, "radius": 0.2 * mm});
            skCircle(sketch, "E131.MirrorC", {"center": v(2.2, -9.35) * mm, "radius": 0.2 * mm});
            skCircle(sketch, "E132.MirrorC", {"center": v(5.5, -5.5) * mm, "radius": 0.2 * mm});
            skCircle(sketch, "E133.MirrorC", {"center": v(4.95, -5.5) * mm, "radius": 0.2 * mm});
            skCircle(sketch, "E134.MirrorC", {"center": v(4.4, -6.05) * mm, "radius": 0.2 * mm});
            skCircle(sketch, "E135.MirrorC", {"center": v(3.85, -6.6) * mm, "radius": 0.2 * mm});
            skCircle(sketch, "E136.MirrorC", {"center": v(8.25, -2.2) * mm, "radius": 0.2 * mm});
            skCircle(sketch, "E137.MirrorC", {"center": v(1.65, -1.1) * mm, "radius": 0.2 * mm});
            skCircle(sketch, "E138.MirrorC", {"center": v(8.8, -3.85) * mm, "radius": 0.2 * mm});
            skCircle(sketch, "E139.MirrorC", {"center": v(1.1, -2.2) * mm, "radius": 0.2 * mm});
            skCircle(sketch, "E140.MirrorC", {"center": v(6.6, -6.05) * mm, "radius": 0.2 * mm});
            skCircle(sketch, "E141.MirrorC", {"center": v(2.75, -7.7) * mm, "radius": 0.2 * mm});
            skCircle(sketch, "E142.MirrorC", {"center": v(3.3, -6.6) * mm, "radius": 0.2 * mm});
            skCircle(sketch, "E143.MirrorC", {"center": v(2.2, -8.8) * mm, "radius": 0.2 * mm});
            skCircle(sketch, "E144.MirrorC", {"center": v(6.05, -5.5) * mm, "radius": 0.2 * mm});
            skCircle(sketch, "E145.MirrorC", {"center": v(7.7, -3.85) * mm, "radius": 0.2 * mm});
            skCircle(sketch, "E146.MirrorC", {"center": v(5.5, -4.95) * mm, "radius": 0.2 * mm});
            skCircle(sketch, "E147.MirrorC", {"center": v(4.95, -4.95) * mm, "radius": 0.2 * mm});
            skCircle(sketch, "E148.MirrorC", {"center": v(4.4, -5.5) * mm, "radius": 0.2 * mm});
            skCircle(sketch, "E149.MirrorC", {"center": v(8.25, -1.65) * mm, "radius": 0.2 * mm});
            skCircle(sketch, "E150.MirrorC", {"center": v(7.15, -6.6) * mm, "radius": 0.2 * mm});
            skCircle(sketch, "E151.MirrorC", {"center": v(3.85, -6.05) * mm, "radius": 0.2 * mm});
            skCircle(sketch, "E152.MirrorC", {"center": v(7.15, -2.2) * mm, "radius": 0.2 * mm});
            skCircle(sketch, "E153.MirrorC", {"center": v(6.6, -4.4) * mm, "radius": 0.2 * mm});
            skCircle(sketch, "E154.MirrorC", {"center": v(7.15, -5.5) * mm, "radius": 0.2 * mm});
            skCircle(sketch, "E155.MirrorC", {"center": v(6.05, -3.85) * mm, "radius": 0.2 * mm});
            skCircle(sketch, "E156.MirrorC", {"center": v(8.8, -3.3) * mm, "radius": 0.2 * mm});
            skCircle(sketch, "E157.MirrorC", {"center": v(7.15, -2.75) * mm, "radius": 0.2 * mm});
            skCircle(sketch, "E158.MirrorC", {"center": v(7.7, -4.4) * mm, "radius": 0.2 * mm});
            skCircle(sketch, "E159.MirrorC", {"center": v(4.95, -1.1) * mm, "radius": 0.2 * mm});
            skCircle(sketch, "E160.MirrorC", {"center": v(5.5, -1.1) * mm, "radius": 0.2 * mm});
            skCircle(sketch, "E161.MirrorC", {"center": v(6.05, -1.1) * mm, "radius": 0.2 * mm});
            skCircle(sketch, "E162.MirrorC", {"center": v(6.6, -1.65) * mm, "radius": 0.2 * mm});
            skCircle(sketch, "E163.MirrorC", {"center": v(2.75, -3.85) * mm, "radius": 0.2 * mm});
            skCircle(sketch, "E164.MirrorC", {"center": v(3.85, -2.2) * mm, "radius": 0.2 * mm});
            skCircle(sketch, "E165.MirrorC", {"center": v(3.3, -2.75) * mm, "radius": 0.2 * mm});
            skCircle(sketch, "E166.MirrorC", {"center": v(4.4, -1.65) * mm, "radius": 0.2 * mm});
            skCircle(sketch, "E167.MirrorC", {"center": v(1.1, -7.15) * mm, "radius": 0.2 * mm});
            skCircle(sketch, "E168.MirrorC", {"center": v(1.65, -6.05) * mm, "radius": 0.2 * mm});
            skCircle(sketch, "E169.MirrorC", {"center": v(2.2, -4.95) * mm, "radius": 0.2 * mm});
            skCircle(sketch, "E170.MirrorC", {"center": v(6.6, -1.1) * mm, "radius": 0.2 * mm});
            skCircle(sketch, "E171.MirrorC", {"center": v(2.75, -3.3) * mm, "radius": 0.2 * mm});
            skCircle(sketch, "E172.MirrorC", {"center": v(3.3, -2.2) * mm, "radius": 0.2 * mm});
            skCircle(sketch, "E173.MirrorC", {"center": v(3.85, -1.65) * mm, "radius": 0.2 * mm});
            skCircle(sketch, "E174.MirrorC", {"center": v(4.4, -1.1) * mm, "radius": 0.2 * mm});
            skCircle(sketch, "E175.MirrorC", {"center": v(1.1, -6.6) * mm, "radius": 0.2 * mm});
            skCircle(sketch, "E176.MirrorC", {"center": v(2.2, -2.2) * mm, "radius": 0.2 * mm});
            skCircle(sketch, "E177.MirrorC", {"center": v(1.1, -4.4) * mm, "radius": 0.2 * mm});
            skCircle(sketch, "E178.MirrorC", {"center": v(2.75, -1.1) * mm, "radius": 0.2 * mm});
            skCircle(sketch, "E179.MirrorC", {"center": v(1.65, -3.3) * mm, "radius": 0.2 * mm});
            skCircle(sketch, "E180.MirrorC", {"center": v(4.4, -7.7) * mm, "radius": 0.2 * mm});
            skCircle(sketch, "E181.MirrorC", {"center": v(3.85, -8.25) * mm, "radius": 0.2 * mm});
            skCircle(sketch, "E182.MirrorC", {"center": v(7.7, -1.1) * mm, "radius": 0.2 * mm});
            skCircle(sketch, "E183.MirrorC", {"center": v(4.95, -7.15) * mm, "radius": 0.2 * mm});
            skCircle(sketch, "E184.MirrorC", {"center": v(5.5, -7.15) * mm, "radius": 0.2 * mm});
            skCircle(sketch, "E185.MirrorC", {"center": v(1.1, -1.65) * mm, "radius": 0.2 * mm});
            skCircle(sketch, "E186.MirrorC", {"center": v(6.6, -7.15) * mm, "radius": 0.2 * mm});
            skCircle(sketch, "E187.MirrorC", {"center": v(8.25, -3.3) * mm, "radius": 0.2 * mm});
            skCircle(sketch, "E188.MirrorC", {"center": v(4.4, -7.15) * mm, "radius": 0.2 * mm});
            skCircle(sketch, "E189.MirrorC", {"center": v(9.35, -1.1) * mm, "radius": 0.2 * mm});
            skCircle(sketch, "E190.MirrorC", {"center": v(4.95, -6.6) * mm, "radius": 0.2 * mm});
            skCircle(sketch, "E191.MirrorC", {"center": v(5.5, -6.6) * mm, "radius": 0.2 * mm});
            skCircle(sketch, "E192.MirrorC", {"center": v(6.05, -6.6) * mm, "radius": 0.2 * mm});
            skCircle(sketch, "E193.MirrorC", {"center": v(2.75, -9.35) * mm, "radius": 0.2 * mm});
            skCircle(sketch, "E194.MirrorC", {"center": v(3.3, -8.25) * mm, "radius": 0.2 * mm});
            skCircle(sketch, "E195.MirrorC", {"center": v(3.85, -7.7) * mm, "radius": 0.2 * mm});
            skCircle(sketch, "E196.MirrorC", {"center": v(1.1, -3.85) * mm, "radius": 0.2 * mm});
            skCircle(sketch, "E197.MirrorC", {"center": v(3.3, -8.8) * mm, "radius": 0.2 * mm});
            skCircle(sketch, "E198.MirrorC", {"center": v(7.7, -1.65) * mm, "radius": 0.2 * mm});
            skCircle(sketch, "E199.MirrorC", {"center": v(1.65, -5.5) * mm, "radius": 0.2 * mm});
            skCircle(sketch, "E200.MirrorC", {"center": v(8.25, -3.85) * mm, "radius": 0.2 * mm});
            skCircle(sketch, "E201.MirrorC", {"center": v(1.65, -2.75) * mm, "radius": 0.2 * mm});
            skCircle(sketch, "E202.MirrorC", {"center": v(2.2, -4.4) * mm, "radius": 0.2 * mm});
            skCircle(sketch, "E203.MirrorC", {"center": v(9.35, -1.65) * mm, "radius": 0.2 * mm});
            skCircle(sketch, "E204.MirrorC", {"center": v(2.2, -1.65) * mm, "radius": 0.2 * mm});
            skCircle(sketch, "E205.MirrorC", {"center": v(6.05, -7.15) * mm, "radius": 0.2 * mm});
            skLineSegment(sketch, "E206.MirrorCS", {"start": v(0, 0) * mm, "end": v(0, -0.55) * mm, "construction": true});
            skCircle(sketch, "E207.MirrorC", {"center": v(0, -0.55) * mm, "radius": 0.2 * mm});
            skCircle(sketch, "E208.MirrorC", {"center": v(1.1, -0.55) * mm, "radius": 0.2 * mm});
            skCircle(sketch, "E209.MirrorC", {"center": v(7.7, -0.55) * mm, "radius": 0.2 * mm});
            skCircle(sketch, "E210.MirrorC", {"center": v(9.35, -0.55) * mm, "radius": 0.2 * mm});
            skCircle(sketch, "E211.MirrorC", {"center": v(8.8, -0.55) * mm, "radius": 0.2 * mm});
            skCircle(sketch, "E212.MirrorC", {"center": v(9.9, -0.55) * mm, "radius": 0.2 * mm});
            skCircle(sketch, "E213.MirrorC", {"center": v(4.95, -0.55) * mm, "radius": 0.2 * mm});
            skCircle(sketch, "E214.MirrorC", {"center": v(5.5, -0.55) * mm, "radius": 0.2 * mm});
            skCircle(sketch, "E215.MirrorC", {"center": v(6.05, -0.55) * mm, "radius": 0.2 * mm});
            skCircle(sketch, "E216.MirrorC", {"center": v(0.55, -0.55) * mm, "radius": 0.2 * mm});
            skCircle(sketch, "E217.MirrorC", {"center": v(6.6, -0.55) * mm, "radius": 0.2 * mm});
            skCircle(sketch, "E218.MirrorC", {"center": v(3.85, -0.55) * mm, "radius": 0.2 * mm});
            skCircle(sketch, "E219.MirrorC", {"center": v(4.4, -0.55) * mm, "radius": 0.2 * mm});
            skCircle(sketch, "E220.MirrorC", {"center": v(7.15, -0.55) * mm, "radius": 0.2 * mm});
            skCircle(sketch, "E221.MirrorC", {"center": v(3.3, -0.55) * mm, "radius": 0.2 * mm});
            skCircle(sketch, "E222.MirrorC", {"center": v(1.65, -0.55) * mm, "radius": 0.2 * mm});
            skCircle(sketch, "E223.MirrorC", {"center": v(8.25, -0.55) * mm, "radius": 0.2 * mm});
            skCircle(sketch, "E224.MirrorC", {"center": v(2.75, -0.55) * mm, "radius": 0.2 * mm});
            skCircle(sketch, "E225.MirrorC", {"center": v(2.2, -0.55) * mm, "radius": 0.2 * mm});
            skCircle(sketch, "E226.MirrorC", {"center": v(0, -7.15) * mm, "radius": 0.2 * mm});
            skCircle(sketch, "E227.MirrorC", {"center": v(0, -7.7) * mm, "radius": 0.2 * mm});
            skCircle(sketch, "E228.MirrorC", {"center": v(0, -8.25) * mm, "radius": 0.2 * mm});
            skCircle(sketch, "E229.MirrorC", {"center": v(0, -1.1) * mm, "radius": 0.2 * mm});
            skCircle(sketch, "E230.MirrorC", {"center": v(0, -1.65) * mm, "radius": 0.2 * mm});
            skCircle(sketch, "E231.MirrorC", {"center": v(0, -2.2) * mm, "radius": 0.2 * mm});
            skCircle(sketch, "E232.MirrorC", {"center": v(0, -2.75) * mm, "radius": 0.2 * mm});
            skCircle(sketch, "E233.MirrorC", {"center": v(0, -3.3) * mm, "radius": 0.2 * mm});
            skCircle(sketch, "E234.MirrorC", {"center": v(0, -3.85) * mm, "radius": 0.2 * mm});
            skCircle(sketch, "E235.MirrorC", {"center": v(0, -4.4) * mm, "radius": 0.2 * mm});
            skCircle(sketch, "E236.MirrorC", {"center": v(0, -4.95) * mm, "radius": 0.2 * mm});
            skCircle(sketch, "E237.MirrorC", {"center": v(0, -5.5) * mm, "radius": 0.2 * mm});
            skCircle(sketch, "E238.MirrorC", {"center": v(0, -6.6) * mm, "radius": 0.2 * mm});
            skCircle(sketch, "E239.MirrorC", {"center": v(0, -6.05) * mm, "radius": 0.2 * mm});
            skCircle(sketch, "E240.MirrorC", {"center": v(0, -8.8) * mm, "radius": 0.2 * mm});
            skCircle(sketch, "E241.MirrorC", {"center": v(0, -9.35) * mm, "radius": 0.2 * mm});
            skCircle(sketch, "E242.MirrorC", {"center": v(0, -9.9) * mm, "radius": 0.2 * mm});
            skCircle(sketch, "E243.MirrorC", {"center": v(0.55, -2.2) * mm, "radius": 0.2 * mm});
            skCircle(sketch, "E244.MirrorC", {"center": v(0.55, -8.25) * mm, "radius": 0.2 * mm});
            skCircle(sketch, "E245.MirrorC", {"center": v(0.55, -7.7) * mm, "radius": 0.2 * mm});
            skCircle(sketch, "E246.MirrorC", {"center": v(0.55, -5.5) * mm, "radius": 0.2 * mm});
            skCircle(sketch, "E247.MirrorC", {"center": v(0.55, -3.85) * mm, "radius": 0.2 * mm});
            skCircle(sketch, "E248.MirrorC", {"center": v(0.55, -6.05) * mm, "radius": 0.2 * mm});
            skCircle(sketch, "E249.MirrorC", {"center": v(0.55, -3.3) * mm, "radius": 0.2 * mm});
            skCircle(sketch, "E250.MirrorC", {"center": v(0.55, -6.6) * mm, "radius": 0.2 * mm});
            skCircle(sketch, "E251.MirrorC", {"center": v(0.55, -4.95) * mm, "radius": 0.2 * mm});
            skCircle(sketch, "E252.MirrorC", {"center": v(0.55, -9.35) * mm, "radius": 0.2 * mm});
            skCircle(sketch, "E253.MirrorC", {"center": v(0.55, -4.4) * mm, "radius": 0.2 * mm});
            skCircle(sketch, "E254.MirrorC", {"center": v(0.55, -9.9) * mm, "radius": 0.2 * mm});
            skCircle(sketch, "E255.MirrorC", {"center": v(0.55, -7.15) * mm, "radius": 0.2 * mm});
            skCircle(sketch, "E256.MirrorC", {"center": v(0.55, -2.75) * mm, "radius": 0.2 * mm});
            skCircle(sketch, "E257.MirrorC", {"center": v(0.55, -8.8) * mm, "radius": 0.2 * mm});
            skCircle(sketch, "E258.MirrorC", {"center": v(0.55, -1.65) * mm, "radius": 0.2 * mm});
            skCircle(sketch, "E259.MirrorC", {"center": v(0.55, -1.1) * mm, "radius": 0.2 * mm});
            skCircle(sketch, "E260.MirrorC", {"center": v(-1.1, -1.1) * mm, "radius": 0.2 * mm});
            skLineSegment(sketch, "E261.MirrorCS", {"start": v(0, 0) * mm, "end": v(-0.55, 0) * mm, "construction": true});
            skCircle(sketch, "E262.MirrorC", {"center": v(-0.55, -0.55) * mm, "radius": 0.2 * mm});
            skCircle(sketch, "E263.MirrorC", {"center": v(-1.1, -0.55) * mm, "radius": 0.2 * mm});
            skCircle(sketch, "E264.MirrorC", {"center": v(-7.7, 1.65) * mm, "radius": 0.2 * mm});
            skCircle(sketch, "E265.MirrorC", {"center": v(-0.55, 6.05) * mm, "radius": 0.2 * mm});
            skCircle(sketch, "E266.MirrorC", {"center": v(-3.85, 8.25) * mm, "radius": 0.2 * mm});
            skCircle(sketch, "E267.MirrorC", {"center": v(-5.5, 2.75) * mm, "radius": 0.2 * mm});
            skCircle(sketch, "E268.MirrorC", {"center": v(-2.75, 2.75) * mm, "radius": 0.2 * mm});
            skCircle(sketch, "E269.MirrorC", {"center": v(-3.3, 1.65) * mm, "radius": 0.2 * mm});
            skCircle(sketch, "E270.MirrorC", {"center": v(-4.4, 0.55) * mm, "radius": 0.2 * mm});
            skCircle(sketch, "E271.MirrorC", {"center": v(-0.55, 7.7) * mm, "radius": 0.2 * mm});
            skCircle(sketch, "E272.MirrorC", {"center": v(-6.05, -3.3) * mm, "radius": 0.2 * mm});
            skCircle(sketch, "E273.MirrorC", {"center": v(-2.2, 3.85) * mm, "radius": 0.2 * mm});
            skCircle(sketch, "E274.MirrorC", {"center": v(-7.15, 2.75) * mm, "radius": 0.2 * mm});
            skCircle(sketch, "E275.MirrorC", {"center": v(-0.55, -7.7) * mm, "radius": 0.2 * mm});
            skCircle(sketch, "E276.MirrorC", {"center": v(-2.2, 9.35) * mm, "radius": 0.2 * mm});
            skCircle(sketch, "E277.MirrorC", {"center": v(-1.1, 2.75) * mm, "radius": 0.2 * mm});
            skCircle(sketch, "E278.MirrorC", {"center": v(-3.85, 1.1) * mm, "radius": 0.2 * mm});
            skCircle(sketch, "E279.MirrorC", {"center": v(-3.3, 2.2) * mm, "radius": 0.2 * mm});
            skCircle(sketch, "E280.MirrorC", {"center": v(-8.25, -5.5) * mm, "radius": 0.2 * mm});
            skCircle(sketch, "E281.MirrorC", {"center": v(-0.55, 2.2) * mm, "radius": 0.2 * mm});
            skCircle(sketch, "E282.MirrorC", {"center": v(-7.7, -4.4) * mm, "radius": 0.2 * mm});
            skCircle(sketch, "E283.MirrorC", {"center": v(-0.55, -4.4) * mm, "radius": 0.2 * mm});
            skCircle(sketch, "E284.MirrorC", {"center": v(-2.75, -6.05) * mm, "radius": 0.2 * mm});
            skCircle(sketch, "E285.MirrorC", {"center": v(-6.05, -7.15) * mm, "radius": 0.2 * mm});
            skCircle(sketch, "E286.MirrorC", {"center": v(-3.85, -1.65) * mm, "radius": 0.2 * mm});
            skCircle(sketch, "E287.MirrorC", {"center": v(-9.35, -1.1) * mm, "radius": 0.2 * mm});
            skCircle(sketch, "E288.MirrorC", {"center": v(-7.15, -2.75) * mm, "radius": 0.2 * mm});
            skCircle(sketch, "E289.MirrorC", {"center": v(-2.2, -7.7) * mm, "radius": 0.2 * mm});
            skCircle(sketch, "E290.MirrorC", {"center": v(-1.1, -7.7) * mm, "radius": 0.2 * mm});
            skCircle(sketch, "E291.MirrorC", {"center": v(-6.6, -6.6) * mm, "radius": 0.2 * mm});
            skCircle(sketch, "E292.MirrorC", {"center": v(-1.65, -4.4) * mm, "radius": 0.2 * mm});
            skCircle(sketch, "E293.MirrorC", {"center": v(-2.75, -4.95) * mm, "radius": 0.2 * mm});
            skCircle(sketch, "E294.MirrorC", {"center": v(-2.75, -2.75) * mm, "radius": 0.2 * mm});
            skCircle(sketch, "E295.MirrorC", {"center": v(-1.1, -9.35) * mm, "radius": 0.2 * mm});
            skCircle(sketch, "E296.MirrorC", {"center": v(-7.15, 1.65) * mm, "radius": 0.2 * mm});
            skCircle(sketch, "E297.MirrorC", {"center": v(-7.7, 3.3) * mm, "radius": 0.2 * mm});
            skCircle(sketch, "E298.MirrorC", {"center": v(-9.35, 3.3) * mm, "radius": 0.2 * mm});
            skCircle(sketch, "E299.MirrorC", {"center": v(-1.1, 4.4) * mm, "radius": 0.2 * mm});
            skCircle(sketch, "E300.MirrorC", {"center": v(-5.5, 0) * mm, "radius": 0.2 * mm});
            skCircle(sketch, "E301.MirrorC", {"center": v(-6.05, 0) * mm, "radius": 0.2 * mm});
            skCircle(sketch, "E302.MirrorC", {"center": v(-6.6, 0.55) * mm, "radius": 0.2 * mm});
            skCircle(sketch, "E303.MirrorC", {"center": v(-2.75, 0) * mm, "radius": 0.2 * mm});
            skCircle(sketch, "E304.MirrorC", {"center": v(-6.05, -7.7) * mm, "radius": 0.2 * mm});
            skCircle(sketch, "E305.MirrorC", {"center": v(-3.3, -6.05) * mm, "radius": 0.2 * mm});
            skCircle(sketch, "E306.MirrorC", {"center": v(-8.25, -1.1) * mm, "radius": 0.2 * mm});
            skCircle(sketch, "E307.MirrorC", {"center": v(-2.2, -8.8) * mm, "radius": 0.2 * mm});
            skCircle(sketch, "E308.MirrorC", {"center": v(-1.1, 2.2) * mm, "radius": 0.2 * mm});
            skCircle(sketch, "E309.MirrorC", {"center": v(-8.25, 0) * mm, "radius": 0.2 * mm});
            skCircle(sketch, "E310.MirrorC", {"center": v(-0.55, 4.4) * mm, "radius": 0.2 * mm});
            skCircle(sketch, "E311.MirrorC", {"center": v(-3.3, 2.75) * mm, "radius": 0.2 * mm});
            skCircle(sketch, "E312.MirrorC", {"center": v(-4.95, 4.4) * mm, "radius": 0.2 * mm});
            skCircle(sketch, "E313.MirrorC", {"center": v(-2.75, 4.4) * mm, "radius": 0.2 * mm});
            skCircle(sketch, "E314.MirrorC", {"center": v(-2.75, 7.15) * mm, "radius": 0.2 * mm});
            skCircle(sketch, "E315.MirrorC", {"center": v(-6.6, 1.1) * mm, "radius": 0.2 * mm});
            skCircle(sketch, "E316.MirrorC", {"center": v(-0.55, -9.35) * mm, "radius": 0.2 * mm});
            skCircle(sketch, "E317.MirrorC", {"center": v(-5.5, -0.55) * mm, "radius": 0.2 * mm});
            skCircle(sketch, "E318.MirrorC", {"center": v(-3.3, -4.95) * mm, "radius": 0.2 * mm});
            skCircle(sketch, "E319.MirrorC", {"center": v(-1.65, 0) * mm, "radius": 0.2 * mm});
            skCircle(sketch, "E320.MirrorC", {"center": v(-2.75, 1.65) * mm, "radius": 0.2 * mm});
            skCircle(sketch, "E321.MirrorC", {"center": v(-1.1, 5.5) * mm, "radius": 0.2 * mm});
            skCircle(sketch, "E322.MirrorC", {"center": v(-0.55, 7.15) * mm, "radius": 0.2 * mm});
            skCircle(sketch, "E323.MirrorC", {"center": v(-1.65, 4.4) * mm, "radius": 0.2 * mm});
            skCircle(sketch, "E324.MirrorC", {"center": v(-2.2, 3.3) * mm, "radius": 0.2 * mm});
            skCircle(sketch, "E325.MirrorC", {"center": v(-6.05, 4.95) * mm, "radius": 0.2 * mm});
            skCircle(sketch, "E326.MirrorC", {"center": v(-2.2, 7.7) * mm, "radius": 0.2 * mm});
            skCircle(sketch, "E327.MirrorC", {"center": v(-1.65, 2.2) * mm, "radius": 0.2 * mm});
            skCircle(sketch, "E328.MirrorC", {"center": v(-3.85, -3.85) * mm, "radius": 0.2 * mm});
            skCircle(sketch, "E329.MirrorC", {"center": v(-7.15, 4.4) * mm, "radius": 0.2 * mm});
            skCircle(sketch, "E330.MirrorC", {"center": v(-4.95, -3.85) * mm, "radius": 0.2 * mm});
            skCircle(sketch, "E331.MirrorC", {"center": v(-2.2, 6.6) * mm, "radius": 0.2 * mm});
            skCircle(sketch, "E332.MirrorC", {"center": v(-1.1, -8.8) * mm, "radius": 0.2 * mm});
            skCircle(sketch, "E333.MirrorC", {"center": v(-3.85, 4.4) * mm, "radius": 0.2 * mm});
            skCircle(sketch, "E334.MirrorC", {"center": v(-8.8, -0.55) * mm, "radius": 0.2 * mm});
            skCircle(sketch, "E335.MirrorC", {"center": v(-3.3, -2.2) * mm, "radius": 0.2 * mm});
            skCircle(sketch, "E336.MirrorC", {"center": v(-4.4, -7.15) * mm, "radius": 0.2 * mm});
            skCircle(sketch, "E337.MirrorC", {"center": v(-2.2, -1.65) * mm, "radius": 0.2 * mm});
            skCircle(sketch, "E338.MirrorC", {"center": v(-7.15, -0.55) * mm, "radius": 0.2 * mm});
            skCircle(sketch, "E339.MirrorC", {"center": v(-8.8, -3.3) * mm, "radius": 0.2 * mm});
            skCircle(sketch, "E340.MirrorC", {"center": v(-6.6, -6.05) * mm, "radius": 0.2 * mm});
            skCircle(sketch, "E341.MirrorC", {"center": v(-2.75, -6.6) * mm, "radius": 0.2 * mm});
            skCircle(sketch, "E342.MirrorC", {"center": v(-8.25, -2.75) * mm, "radius": 0.2 * mm});
            skCircle(sketch, "E343.MirrorC", {"center": v(-2.2, -3.3) * mm, "radius": 0.2 * mm});
            skCircle(sketch, "E344.MirrorC", {"center": v(-3.85, -3.3) * mm, "radius": 0.2 * mm});
            skCircle(sketch, "E345.MirrorC", {"center": v(-3.85, -1.1) * mm, "radius": 0.2 * mm});
            skCircle(sketch, "E346.MirrorC", {"center": v(-7.15, -4.4) * mm, "radius": 0.2 * mm});
            skCircle(sketch, "E347.MirrorC", {"center": v(-7.15, 1.1) * mm, "radius": 0.2 * mm});
            skCircle(sketch, "E348.MirrorC", {"center": v(-7.7, 2.75) * mm, "radius": 0.2 * mm});
            skCircle(sketch, "E349.MirrorC", {"center": v(-8.25, 4.95) * mm, "radius": 0.2 * mm});
            skCircle(sketch, "E350.MirrorC", {"center": v(-9.35, 2.75) * mm, "radius": 0.2 * mm});
            skCircle(sketch, "E351.MirrorC", {"center": v(-4.4, 8.8) * mm, "radius": 0.2 * mm});
            skCircle(sketch, "E352.MirrorC", {"center": v(-4.95, 8.25) * mm, "radius": 0.2 * mm});
            skCircle(sketch, "E353.MirrorC", {"center": v(-5.5, 8.25) * mm, "radius": 0.2 * mm});
            skCircle(sketch, "E354.MirrorC", {"center": v(-6.6, 0) * mm, "radius": 0.2 * mm});
            skCircle(sketch, "E355.MirrorC", {"center": v(-2.75, 2.2) * mm, "radius": 0.2 * mm});
            skCircle(sketch, "E356.MirrorC", {"center": v(-3.85, 0.55) * mm, "radius": 0.2 * mm});
            skCircle(sketch, "E357.MirrorC", {"center": v(-3.85, -8.25) * mm, "radius": 0.2 * mm});
            skCircle(sketch, "E358.MirrorC", {"center": v(-4.4, 0) * mm, "radius": 0.2 * mm});
            skCircle(sketch, "E359.MirrorC", {"center": v(-3.3, -8.8) * mm, "radius": 0.2 * mm});
            skCircle(sketch, "E360.MirrorC", {"center": v(-3.3, -7.7) * mm, "radius": 0.2 * mm});
            skCircle(sketch, "E361.MirrorC", {"center": v(-7.15, 0) * mm, "radius": 0.2 * mm});
            skCircle(sketch, "E362.MirrorC", {"center": v(-1.1, -2.2) * mm, "radius": 0.2 * mm});
            skCircle(sketch, "E363.MirrorC", {"center": v(-3.3, -5.5) * mm, "radius": 0.2 * mm});
            skCircle(sketch, "E364.MirrorC", {"center": v(-1.65, -9.35) * mm, "radius": 0.2 * mm});
            skCircle(sketch, "E365.MirrorC", {"center": v(-3.85, -7.15) * mm, "radius": 0.2 * mm});
            skCircle(sketch, "E366.MirrorC", {"center": v(-3.3, -3.3) * mm, "radius": 0.2 * mm});
            skCircle(sketch, "E367.MirrorC", {"center": v(-4.4, -2.75) * mm, "radius": 0.2 * mm});
            skCircle(sketch, "E368.MirrorC", {"center": v(-7.7, -2.2) * mm, "radius": 0.2 * mm});
            skCircle(sketch, "E369.MirrorC", {"center": v(-6.6, -4.95) * mm, "radius": 0.2 * mm});
            skCircle(sketch, "E370.MirrorC", {"center": v(-1.1, -6.05) * mm, "radius": 0.2 * mm});
            skCircle(sketch, "E371.MirrorC", {"center": v(-7.7, -1.65) * mm, "radius": 0.2 * mm});
            skCircle(sketch, "E372.MirrorC", {"center": v(-3.3, -0.55) * mm, "radius": 0.2 * mm});
            skCircle(sketch, "E373.MirrorC", {"center": v(-7.7, -6.05) * mm, "radius": 0.2 * mm});
            skCircle(sketch, "E374.MirrorC", {"center": v(-7.7, 2.2) * mm, "radius": 0.2 * mm});
            skCircle(sketch, "E375.MirrorC", {"center": v(-5.5, -2.75) * mm, "radius": 0.2 * mm});
            skCircle(sketch, "E376.MirrorC", {"center": v(-9.35, 2.2) * mm, "radius": 0.2 * mm});
            skCircle(sketch, "E377.MirrorC", {"center": v(-8.25, 4.4) * mm, "radius": 0.2 * mm});
            skCircle(sketch, "E378.MirrorC", {"center": v(-4.4, 8.25) * mm, "radius": 0.2 * mm});
            skCircle(sketch, "E379.MirrorC", {"center": v(-3.3, 0.55) * mm, "radius": 0.2 * mm});
            skCircle(sketch, "E380.MirrorC", {"center": v(-3.85, 8.8) * mm, "radius": 0.2 * mm});
            skCircle(sketch, "E381.MirrorC", {"center": v(-1.1, 4.95) * mm, "radius": 0.2 * mm});
            skCircle(sketch, "E382.MirrorC", {"center": v(-1.65, 3.85) * mm, "radius": 0.2 * mm});
            skCircle(sketch, "E383.MirrorC", {"center": v(-2.2, 2.75) * mm, "radius": 0.2 * mm});
            skCircle(sketch, "E384.MirrorC", {"center": v(-6.05, 2.75) * mm, "radius": 0.2 * mm});
            skCircle(sketch, "E385.MirrorC", {"center": v(-2.2, 7.15) * mm, "radius": 0.2 * mm});
            skCircle(sketch, "E386.MirrorC", {"center": v(-7.15, -6.05) * mm, "radius": 0.2 * mm});
            skCircle(sketch, "E387.MirrorC", {"center": v(-1.65, 6.05) * mm, "radius": 0.2 * mm});
            skCircle(sketch, "E388.MirrorC", {"center": v(-2.75, -8.8) * mm, "radius": 0.2 * mm});
            skCircle(sketch, "E389.MirrorC", {"center": v(-2.75, -7.15) * mm, "radius": 0.2 * mm});
            skCircle(sketch, "E390.MirrorC", {"center": v(-3.85, 0) * mm, "radius": 0.2 * mm});
            skCircle(sketch, "E391.MirrorC", {"center": v(-2.75, -7.7) * mm, "radius": 0.2 * mm});
            skCircle(sketch, "E392.MirrorC", {"center": v(-3.85, -4.4) * mm, "radius": 0.2 * mm});
            skCircle(sketch, "E393.MirrorC", {"center": v(-4.95, 6.05) * mm, "radius": 0.2 * mm});
            skCircle(sketch, "E394.MirrorC", {"center": v(-0.55, 6.6) * mm, "radius": 0.2 * mm});
            skCircle(sketch, "E395.MirrorC", {"center": v(-4.95, -7.15) * mm, "radius": 0.2 * mm});
            skCircle(sketch, "E396.MirrorC", {"center": v(-5.5, 7.7) * mm, "radius": 0.2 * mm});
            skCircle(sketch, "E397.MirrorC", {"center": v(-0.55, -8.25) * mm, "radius": 0.2 * mm});
            skCircle(sketch, "E398.MirrorC", {"center": v(-2.75, -3.3) * mm, "radius": 0.2 * mm});
            skCircle(sketch, "E399.MirrorC", {"center": v(-8.25, -3.3) * mm, "radius": 0.2 * mm});
            skCircle(sketch, "E400.MirrorC", {"center": v(-9.35, -1.65) * mm, "radius": 0.2 * mm});
            skCircle(sketch, "E401.MirrorC", {"center": v(-4.4, -0.55) * mm, "radius": 0.2 * mm});
            skCircle(sketch, "E402.MirrorC", {"center": v(-6.05, -3.85) * mm, "radius": 0.2 * mm});
            skCircle(sketch, "E403.MirrorC", {"center": v(-7.15, -3.3) * mm, "radius": 0.2 * mm});
            skCircle(sketch, "E404.MirrorC", {"center": v(-3.3, 6.05) * mm, "radius": 0.2 * mm});
            skCircle(sketch, "E405.MirrorC", {"center": v(-9.35, 0.55) * mm, "radius": 0.2 * mm});
            skCircle(sketch, "E406.MirrorC", {"center": v(-1.1, 6.6) * mm, "radius": 0.2 * mm});
            skCircle(sketch, "E407.MirrorC", {"center": v(-4.95, -1.1) * mm, "radius": 0.2 * mm});
            skCircle(sketch, "E408.MirrorC", {"center": v(-5.5, 1.1) * mm, "radius": 0.2 * mm});
            skCircle(sketch, "E409.MirrorC", {"center": v(-8.8, -1.65) * mm, "radius": 0.2 * mm});
            skCircle(sketch, "E410.MirrorC", {"center": v(-1.1, 1.65) * mm, "radius": 0.2 * mm});
            skCircle(sketch, "E411.MirrorC", {"center": v(-4.4, -4.4) * mm, "radius": 0.2 * mm});
            skCircle(sketch, "E412.MirrorC", {"center": v(-8.25, 0.55) * mm, "radius": 0.2 * mm});
            skCircle(sketch, "E413.MirrorC", {"center": v(-7.7, 0) * mm, "radius": 0.2 * mm});
            skCircle(sketch, "E414.MirrorC", {"center": v(-1.1, 0) * mm, "radius": 0.2 * mm});
            skCircle(sketch, "E415.MirrorC", {"center": v(-4.95, -4.4) * mm, "radius": 0.2 * mm});
            skCircle(sketch, "E416.MirrorC", {"center": v(-4.4, -6.6) * mm, "radius": 0.2 * mm});
            skCircle(sketch, "E417.MirrorC", {"center": v(-7.7, -2.75) * mm, "radius": 0.2 * mm});
            skCircle(sketch, "E418.MirrorC", {"center": v(-3.3, -3.85) * mm, "radius": 0.2 * mm});
            skCircle(sketch, "E419.MirrorC", {"center": v(-4.95, -5.5) * mm, "radius": 0.2 * mm});
            skCircle(sketch, "E420.MirrorC", {"center": v(-9.35, 0) * mm, "radius": 0.2 * mm});
            skCircle(sketch, "E421.MirrorC", {"center": v(-1.1, 6.05) * mm, "radius": 0.2 * mm});
            skCircle(sketch, "E422.MirrorC", {"center": v(-2.2, 0.55) * mm, "radius": 0.2 * mm});
            skCircle(sketch, "E423.MirrorC", {"center": v(-3.3, 5.5) * mm, "radius": 0.2 * mm});
            skCircle(sketch, "E424.MirrorC", {"center": v(-3.85, 6.6) * mm, "radius": 0.2 * mm});
            skCircle(sketch, "E425.MirrorC", {"center": v(-5.5, -7.15) * mm, "radius": 0.2 * mm});
            skCircle(sketch, "E426.MirrorC", {"center": v(-3.85, 2.75) * mm, "radius": 0.2 * mm});
            skCircle(sketch, "E427.MirrorC", {"center": v(-5.5, 4.4) * mm, "radius": 0.2 * mm});
            skCircle(sketch, "E428.MirrorC", {"center": v(-7.15, -4.95) * mm, "radius": 0.2 * mm});
            skCircle(sketch, "E429.MirrorC", {"center": v(-4.4, -3.85) * mm, "radius": 0.2 * mm});
            skCircle(sketch, "E430.MirrorC", {"center": v(-1.1, 3.3) * mm, "radius": 0.2 * mm});
            skCircle(sketch, "E431.MirrorC", {"center": v(-8.25, 1.65) * mm, "radius": 0.2 * mm});
            skCircle(sketch, "E432.MirrorC", {"center": v(-2.75, -1.65) * mm, "radius": 0.2 * mm});
            skCircle(sketch, "E433.MirrorC", {"center": v(-2.2, -1.1) * mm, "radius": 0.2 * mm});
            skCircle(sketch, "E434.MirrorC", {"center": v(-3.85, -5.5) * mm, "radius": 0.2 * mm});
            skCircle(sketch, "E435.MirrorC", {"center": v(-2.2, 1.1) * mm, "radius": 0.2 * mm});
            skCircle(sketch, "E436.MirrorC", {"center": v(-8.25, 2.2) * mm, "radius": 0.2 * mm});
            skCircle(sketch, "E437.MirrorC", {"center": v(-8.8, 0) * mm, "radius": 0.2 * mm});
            skCircle(sketch, "E438.MirrorC", {"center": v(-7.15, 2.2) * mm, "radius": 0.2 * mm});
            skCircle(sketch, "E439.MirrorC", {"center": v(-3.3, -1.65) * mm, "radius": 0.2 * mm});
            skCircle(sketch, "E440.MirrorC", {"center": v(-6.6, -2.75) * mm, "radius": 0.2 * mm});
            skCircle(sketch, "E441.MirrorC", {"center": v(-7.15, 3.85) * mm, "radius": 0.2 * mm});
            skCircle(sketch, "E442.MirrorC", {"center": v(-1.1, -5.5) * mm, "radius": 0.2 * mm});
            skCircle(sketch, "E443.MirrorC", {"center": v(-6.05, -6.05) * mm, "radius": 0.2 * mm});
            skCircle(sketch, "E444.MirrorC", {"center": v(-1.65, -6.6) * mm, "radius": 0.2 * mm});
            skCircle(sketch, "E445.MirrorC", {"center": v(-1.65, -8.8) * mm, "radius": 0.2 * mm});
            skCircle(sketch, "E446.MirrorC", {"center": v(-1.65, -0.55) * mm, "radius": 0.2 * mm});
            skCircle(sketch, "E447.MirrorC", {"center": v(-4.95, -6.6) * mm, "radius": 0.2 * mm});
            skCircle(sketch, "E448.MirrorC", {"center": v(-4.4, -1.1) * mm, "radius": 0.2 * mm});
            skCircle(sketch, "E449.MirrorC", {"center": v(-1.1, -6.6) * mm, "radius": 0.2 * mm});
            skCircle(sketch, "E450.MirrorC", {"center": v(-0.55, -9.9) * mm, "radius": 0.2 * mm});
            skCircle(sketch, "E451.MirrorC", {"center": v(-4.95, 1.65) * mm, "radius": 0.2 * mm});
            skCircle(sketch, "E452.MirrorC", {"center": v(-2.2, 4.4) * mm, "radius": 0.2 * mm});
            skCircle(sketch, "E453.MirrorC", {"center": v(-4.4, 6.6) * mm, "radius": 0.2 * mm});
            skCircle(sketch, "E454.MirrorC", {"center": v(-6.05, -5.5) * mm, "radius": 0.2 * mm});
            skCircle(sketch, "E455.MirrorC", {"center": v(-0.55, 8.8) * mm, "radius": 0.2 * mm});
            skCircle(sketch, "E456.MirrorC", {"center": v(-6.05, 2.2) * mm, "radius": 0.2 * mm});
            skCircle(sketch, "E457.MirrorC", {"center": v(-2.2, 4.95) * mm, "radius": 0.2 * mm});
            skCircle(sketch, "E458.MirrorC", {"center": v(-5.5, -3.85) * mm, "radius": 0.2 * mm});
            skCircle(sketch, "E459.MirrorC", {"center": v(-3.85, 3.3) * mm, "radius": 0.2 * mm});
            skCircle(sketch, "E460.MirrorC", {"center": v(-5.5, 1.65) * mm, "radius": 0.2 * mm});
            skCircle(sketch, "E461.MirrorC", {"center": v(-2.75, 7.7) * mm, "radius": 0.2 * mm});
            skCircle(sketch, "E462.MirrorC", {"center": v(-1.65, 5.5) * mm, "radius": 0.2 * mm});
            skCircle(sketch, "E463.MirrorC", {"center": v(-0.55, 8.25) * mm, "radius": 0.2 * mm});
            skCircle(sketch, "E464.MirrorC", {"center": v(-4.4, 1.1) * mm, "radius": 0.2 * mm});
            skCircle(sketch, "E465.MirrorC", {"center": v(-3.85, 1.65) * mm, "radius": 0.2 * mm});
            skCircle(sketch, "E466.MirrorC", {"center": v(-2.75, 3.3) * mm, "radius": 0.2 * mm});
            skCircle(sketch, "E467.MirrorC", {"center": v(-6.05, 0.55) * mm, "radius": 0.2 * mm});
            skCircle(sketch, "E468.MirrorC", {"center": v(-4.95, 0.55) * mm, "radius": 0.2 * mm});
            skCircle(sketch, "E469.MirrorC", {"center": v(-4.4, 1.65) * mm, "radius": 0.2 * mm});
            skCircle(sketch, "E470.MirrorC", {"center": v(-0.55, 2.75) * mm, "radius": 0.2 * mm});
            skCircle(sketch, "E471.MirrorC", {"center": v(-0.55, -1.1) * mm, "radius": 0.2 * mm});
            skCircle(sketch, "E472.MirrorC", {"center": v(-8.8, 2.75) * mm, "radius": 0.2 * mm});
            skCircle(sketch, "E473.MirrorC", {"center": v(-2.2, 0) * mm, "radius": 0.2 * mm});
            skCircle(sketch, "E474.MirrorC", {"center": v(-2.75, -9.35) * mm, "radius": 0.2 * mm});
            skCircle(sketch, "E475.MirrorC", {"center": v(-3.3, 4.4) * mm, "radius": 0.2 * mm});
            skCircle(sketch, "E476.MirrorC", {"center": v(-5.5, -7.7) * mm, "radius": 0.2 * mm});
            skCircle(sketch, "E477.MirrorC", {"center": v(-4.4, -4.95) * mm, "radius": 0.2 * mm});
            skCircle(sketch, "E478.MirrorC", {"center": v(-5.5, -6.05) * mm, "radius": 0.2 * mm});
            skCircle(sketch, "E479.MirrorC", {"center": v(-5.5, -8.25) * mm, "radius": 0.2 * mm});
            skCircle(sketch, "E480.MirrorC", {"center": v(-1.65, -7.7) * mm, "radius": 0.2 * mm});
            skCircle(sketch, "E481.MirrorC", {"center": v(-2.2, -2.75) * mm, "radius": 0.2 * mm});
            skCircle(sketch, "E482.MirrorC", {"center": v(-2.2, -5.5) * mm, "radius": 0.2 * mm});
            skCircle(sketch, "E483.MirrorC", {"center": v(-1.1, -8.25) * mm, "radius": 0.2 * mm});
            skCircle(sketch, "E484.MirrorC", {"center": v(-8.25, -0.55) * mm, "radius": 0.2 * mm});
            skCircle(sketch, "E485.MirrorC", {"center": v(-5.5, -6.6) * mm, "radius": 0.2 * mm});
            skCircle(sketch, "E486.MirrorC", {"center": v(-4.95, -0.55) * mm, "radius": 0.2 * mm});
            skCircle(sketch, "E487.MirrorC", {"center": v(-1.65, -5.5) * mm, "radius": 0.2 * mm});
            skCircle(sketch, "E488.MirrorC", {"center": v(-0.55, -7.15) * mm, "radius": 0.2 * mm});
            skCircle(sketch, "E489.MirrorC", {"center": v(-7.15, 6.05) * mm, "radius": 0.2 * mm});
            skCircle(sketch, "E490.MirrorC", {"center": v(-2.75, -1.1) * mm, "radius": 0.2 * mm});
            skCircle(sketch, "E491.MirrorC", {"center": v(-8.25, -3.85) * mm, "radius": 0.2 * mm});
            skCircle(sketch, "E492.MirrorC", {"center": v(-5.5, 0.55) * mm, "radius": 0.2 * mm});
            skCircle(sketch, "E493.MirrorC", {"center": v(-2.2, -2.2) * mm, "radius": 0.2 * mm});
            skCircle(sketch, "E494.MirrorC", {"center": v(-1.65, 8.8) * mm, "radius": 0.2 * mm});
            skCircle(sketch, "E495.MirrorC", {"center": v(-8.25, 5.5) * mm, "radius": 0.2 * mm});
            skCircle(sketch, "E496.MirrorC", {"center": v(-0.55, -6.6) * mm, "radius": 0.2 * mm});
            skCircle(sketch, "E497.MirrorC", {"center": v(-7.7, 0.55) * mm, "radius": 0.2 * mm});
            skCircle(sketch, "E498.MirrorC", {"center": v(-6.6, -1.1) * mm, "radius": 0.2 * mm});
            skCircle(sketch, "E499.MirrorC", {"center": v(-7.15, -2.2) * mm, "radius": 0.2 * mm});
            skCircle(sketch, "E500.MirrorC", {"center": v(-3.3, 7.15) * mm, "radius": 0.2 * mm});
            skCircle(sketch, "E501.MirrorC", {"center": v(-4.4, -6.05) * mm, "radius": 0.2 * mm});
            skCircle(sketch, "E502.MirrorC", {"center": v(-0.55, -2.2) * mm, "radius": 0.2 * mm});
            skCircle(sketch, "E503.MirrorC", {"center": v(-6.05, -2.75) * mm, "radius": 0.2 * mm});
            skCircle(sketch, "E504.MirrorC", {"center": v(-1.65, -6.05) * mm, "radius": 0.2 * mm});
            skCircle(sketch, "E505.MirrorC", {"center": v(-6.05, 5.5) * mm, "radius": 0.2 * mm});
            skCircle(sketch, "E506.MirrorC", {"center": v(-6.6, 6.05) * mm, "radius": 0.2 * mm});
            skCircle(sketch, "E507.MirrorC", {"center": v(-3.3, -6.6) * mm, "radius": 0.2 * mm});
            skCircle(sketch, "E508.MirrorC", {"center": v(-8.8, -4.4) * mm, "radius": 0.2 * mm});
            skCircle(sketch, "E509.MirrorC", {"center": v(-1.65, 4.95) * mm, "radius": 0.2 * mm});
            skCircle(sketch, "E510.MirrorC", {"center": v(-9.35, 1.65) * mm, "radius": 0.2 * mm});
            skCircle(sketch, "E511.MirrorC", {"center": v(-5.5, 7.15) * mm, "radius": 0.2 * mm});
            skCircle(sketch, "E512.MirrorC", {"center": v(-4.95, 7.15) * mm, "radius": 0.2 * mm});
            skCircle(sketch, "E513.MirrorC", {"center": v(-4.4, 5.5) * mm, "radius": 0.2 * mm});
            skCircle(sketch, "E514.MirrorC", {"center": v(-8.8, 4.4) * mm, "radius": 0.2 * mm});
            skCircle(sketch, "E515.MirrorC", {"center": v(-0.55, -6.05) * mm, "radius": 0.2 * mm});
            skCircle(sketch, "E516.MirrorC", {"center": v(-9.35, -3.3) * mm, "radius": 0.2 * mm});
            skCircle(sketch, "E517.MirrorC", {"center": v(-7.15, 6.6) * mm, "radius": 0.2 * mm});
            skCircle(sketch, "E518.MirrorC", {"center": v(-2.2, -3.85) * mm, "radius": 0.2 * mm});
            skCircle(sketch, "E519.MirrorC", {"center": v(-1.65, 1.1) * mm, "radius": 0.2 * mm});
            skCircle(sketch, "E520.MirrorC", {"center": v(-3.3, -8.25) * mm, "radius": 0.2 * mm});
            skCircle(sketch, "E521.MirrorC", {"center": v(-5.5, -4.95) * mm, "radius": 0.2 * mm});
            skCircle(sketch, "E522.MirrorC", {"center": v(-7.7, -3.3) * mm, "radius": 0.2 * mm});
            skCircle(sketch, "E523.MirrorC", {"center": v(-4.4, 3.85) * mm, "radius": 0.2 * mm});
            skCircle(sketch, "E524.MirrorC", {"center": v(-6.6, -3.3) * mm, "radius": 0.2 * mm});
            skCircle(sketch, "E525.MirrorC", {"center": v(-0.55, 0) * mm, "radius": 0.2 * mm});
            skCircle(sketch, "E526.MirrorC", {"center": v(-1.1, 7.15) * mm, "radius": 0.2 * mm});
            skCircle(sketch, "E527.MirrorC", {"center": v(-3.85, 2.2) * mm, "radius": 0.2 * mm});
            skCircle(sketch, "E528.MirrorC", {"center": v(-2.75, 3.85) * mm, "radius": 0.2 * mm});
            skCircle(sketch, "E529.MirrorC", {"center": v(-6.6, 1.65) * mm, "radius": 0.2 * mm});
            skCircle(sketch, "E530.MirrorC", {"center": v(-6.05, 1.1) * mm, "radius": 0.2 * mm});
            skCircle(sketch, "E531.MirrorC", {"center": v(-4.95, 1.1) * mm, "radius": 0.2 * mm});
            skCircle(sketch, "E532.MirrorC", {"center": v(-9.9, 0.55) * mm, "radius": 0.2 * mm});
            skCircle(sketch, "E533.MirrorC", {"center": v(-8.8, 0.55) * mm, "radius": 0.2 * mm});
            skCircle(sketch, "E534.MirrorC", {"center": v(-1.65, 0.55) * mm, "radius": 0.2 * mm});
            skCircle(sketch, "E535.MirrorC", {"center": v(-3.3, -2.75) * mm, "radius": 0.2 * mm});
            skCircle(sketch, "E536.MirrorC", {"center": v(-1.65, 9.35) * mm, "radius": 0.2 * mm});
            skCircle(sketch, "E537.MirrorC", {"center": v(-4.4, 4.95) * mm, "radius": 0.2 * mm});
            skCircle(sketch, "E538.MirrorC", {"center": v(-6.6, 4.95) * mm, "radius": 0.2 * mm});
            skCircle(sketch, "E539.MirrorC", {"center": v(-6.6, -7.15) * mm, "radius": 0.2 * mm});
            skCircle(sketch, "E540.MirrorC", {"center": v(-8.8, -2.2) * mm, "radius": 0.2 * mm});
            skCircle(sketch, "E541.MirrorC", {"center": v(-4.4, -7.7) * mm, "radius": 0.2 * mm});
            skCircle(sketch, "E542.MirrorC", {"center": v(-1.1, -3.3) * mm, "radius": 0.2 * mm});
            skCircle(sketch, "E543.MirrorC", {"center": v(-5.5, -5.5) * mm, "radius": 0.2 * mm});
            skCircle(sketch, "E544.MirrorC", {"center": v(-3.3, -4.4) * mm, "radius": 0.2 * mm});
            skCircle(sketch, "E545.MirrorC", {"center": v(-2.2, -4.4) * mm, "radius": 0.2 * mm});
            skCircle(sketch, "E546.MirrorC", {"center": v(-3.85, -0.55) * mm, "radius": 0.2 * mm});
            skCircle(sketch, "E547.MirrorC", {"center": v(-7.15, -5.5) * mm, "radius": 0.2 * mm});
            skCircle(sketch, "E548.MirrorC", {"center": v(-8.8, 3.3) * mm, "radius": 0.2 * mm});
            skCircle(sketch, "E549.MirrorC", {"center": v(-2.2, 2.2) * mm, "radius": 0.2 * mm});
            skCircle(sketch, "E550.MirrorC", {"center": v(-0.55, 3.85) * mm, "radius": 0.2 * mm});
            skCircle(sketch, "E551.MirrorC", {"center": v(-8.8, -1.1) * mm, "radius": 0.2 * mm});
            skCircle(sketch, "E552.MirrorC", {"center": v(-8.8, -3.85) * mm, "radius": 0.2 * mm});
            skCircle(sketch, "E553.MirrorC", {"center": v(-3.85, -6.6) * mm, "radius": 0.2 * mm});
            skCircle(sketch, "E554.MirrorC", {"center": v(-0.55, 4.95) * mm, "radius": 0.2 * mm});
            skCircle(sketch, "E555.MirrorC", {"center": v(-2.75, -5.5) * mm, "radius": 0.2 * mm});
            skCircle(sketch, "E556.MirrorC", {"center": v(-4.95, 4.95) * mm, "radius": 0.2 * mm});
            skCircle(sketch, "E557.MirrorC", {"center": v(-1.65, 3.3) * mm, "radius": 0.2 * mm});
            skCircle(sketch, "E558.MirrorC", {"center": v(-0.55, -1.65) * mm, "radius": 0.2 * mm});
            skCircle(sketch, "E559.MirrorC", {"center": v(-1.65, 1.65) * mm, "radius": 0.2 * mm});
            skCircle(sketch, "E560.MirrorC", {"center": v(-7.7, 3.85) * mm, "radius": 0.2 * mm});
            skCircle(sketch, "E561.MirrorC", {"center": v(-4.4, -2.2) * mm, "radius": 0.2 * mm});
            skCircle(sketch, "E562.MirrorC", {"center": v(-7.15, -3.85) * mm, "radius": 0.2 * mm});
            skCircle(sketch, "E563.MirrorC", {"center": v(-4.95, 0) * mm, "radius": 0.2 * mm});
            skCircle(sketch, "E564.MirrorC", {"center": v(-7.15, 0.55) * mm, "radius": 0.2 * mm});
            skCircle(sketch, "E565.MirrorC", {"center": v(-5.5, -2.2) * mm, "radius": 0.2 * mm});
            skCircle(sketch, "E566.MirrorC", {"center": v(-6.05, 3.85) * mm, "radius": 0.2 * mm});
            skCircle(sketch, "E567.MirrorC", {"center": v(-2.2, -6.6) * mm, "radius": 0.2 * mm});
            skCircle(sketch, "E568.MirrorC", {"center": v(-1.65, -1.65) * mm, "radius": 0.2 * mm});
            skCircle(sketch, "E569.MirrorC", {"center": v(-4.95, 7.7) * mm, "radius": 0.2 * mm});
            skCircle(sketch, "E570.MirrorC", {"center": v(-5.5, 4.95) * mm, "radius": 0.2 * mm});
            skCircle(sketch, "E571.MirrorC", {"center": v(-6.05, -0.55) * mm, "radius": 0.2 * mm});
            skCircle(sketch, "E572.MirrorC", {"center": v(-8.25, -1.65) * mm, "radius": 0.2 * mm});
            skCircle(sketch, "E573.MirrorC", {"center": v(-3.3, 0) * mm, "radius": 0.2 * mm});
            skCircle(sketch, "E574.MirrorC", {"center": v(-4.95, -3.3) * mm, "radius": 0.2 * mm});
            skCircle(sketch, "E575.MirrorC", {"center": v(-3.3, 7.7) * mm, "radius": 0.2 * mm});
            skCircle(sketch, "E576.MirrorC", {"center": v(-1.1, 7.7) * mm, "radius": 0.2 * mm});
            skCircle(sketch, "E577.MirrorC", {"center": v(-4.95, -4.95) * mm, "radius": 0.2 * mm});
            skCircle(sketch, "E578.MirrorC", {"center": v(-0.55, -4.95) * mm, "radius": 0.2 * mm});
            skCircle(sketch, "E579.MirrorC", {"center": v(-3.85, 7.15) * mm, "radius": 0.2 * mm});
            skCircle(sketch, "E580.MirrorC", {"center": v(-3.85, 6.05) * mm, "radius": 0.2 * mm});
            skCircle(sketch, "E581.MirrorC", {"center": v(-3.85, 5.5) * mm, "radius": 0.2 * mm});
            skCircle(sketch, "E582.MirrorC", {"center": v(-6.05, 3.3) * mm, "radius": 0.2 * mm});
            skCircle(sketch, "E583.MirrorC", {"center": v(-7.7, -5.5) * mm, "radius": 0.2 * mm});
            skCircle(sketch, "E584.MirrorC", {"center": v(-6.6, 3.85) * mm, "radius": 0.2 * mm});
            skCircle(sketch, "E585.MirrorC", {"center": v(-2.75, -2.2) * mm, "radius": 0.2 * mm});
            skCircle(sketch, "E586.MirrorC", {"center": v(-6.05, 7.7) * mm, "radius": 0.2 * mm});
            skCircle(sketch, "E587.MirrorC", {"center": v(-8.25, 3.85) * mm, "radius": 0.2 * mm});
            skCircle(sketch, "E588.MirrorC", {"center": v(-7.7, -4.95) * mm, "radius": 0.2 * mm});
            skCircle(sketch, "E589.MirrorC", {"center": v(-1.65, -2.2) * mm, "radius": 0.2 * mm});
            skCircle(sketch, "E590.MirrorC", {"center": v(-2.2, -9.35) * mm, "radius": 0.2 * mm});
            skCircle(sketch, "E591.MirrorC", {"center": v(-0.55, 0.55) * mm, "radius": 0.2 * mm});
            skCircle(sketch, "E592.MirrorC", {"center": v(-0.55, -3.85) * mm, "radius": 0.2 * mm});
            skCircle(sketch, "E593.MirrorC", {"center": v(-0.55, 9.35) * mm, "radius": 0.2 * mm});
            skCircle(sketch, "E594.MirrorC", {"center": v(-6.05, -4.95) * mm, "radius": 0.2 * mm});
            skCircle(sketch, "E595.MirrorC", {"center": v(-7.7, -1.1) * mm, "radius": 0.2 * mm});
            skCircle(sketch, "E596.MirrorC", {"center": v(-3.3, 3.3) * mm, "radius": 0.2 * mm});
            skCircle(sketch, "E597.MirrorC", {"center": v(-4.4, 7.7) * mm, "radius": 0.2 * mm});
            skCircle(sketch, "E598.MirrorC", {"center": v(-2.2, -8.25) * mm, "radius": 0.2 * mm});
            skCircle(sketch, "E599.MirrorC", {"center": v(-3.85, -8.8) * mm, "radius": 0.2 * mm});
            skCircle(sketch, "E600.MirrorC", {"center": v(-6.6, 2.2) * mm, "radius": 0.2 * mm});
            skCircle(sketch, "E601.MirrorC", {"center": v(-6.05, 1.65) * mm, "radius": 0.2 * mm});
            skCircle(sketch, "E602.MirrorC", {"center": v(-6.05, -4.4) * mm, "radius": 0.2 * mm});
            skCircle(sketch, "E603.MirrorC", {"center": v(-7.7, 4.95) * mm, "radius": 0.2 * mm});
            skCircle(sketch, "E604.MirrorC", {"center": v(-8.8, 1.1) * mm, "radius": 0.2 * mm});
            skCircle(sketch, "E605.MirrorC", {"center": v(-6.05, -1.1) * mm, "radius": 0.2 * mm});
            skCircle(sketch, "E606.MirrorC", {"center": v(-1.1, -7.15) * mm, "radius": 0.2 * mm});
            skCircle(sketch, "E607.MirrorC", {"center": v(-3.85, 7.7) * mm, "radius": 0.2 * mm});
            skCircle(sketch, "E608.MirrorC", {"center": v(-2.2, -7.15) * mm, "radius": 0.2 * mm});
            skCircle(sketch, "E609.MirrorC", {"center": v(-2.75, -3.85) * mm, "radius": 0.2 * mm});
            skCircle(sketch, "E610.MirrorC", {"center": v(-1.1, 1.1) * mm, "radius": 0.2 * mm});
            skCircle(sketch, "E611.MirrorC", {"center": v(-7.15, -6.6) * mm, "radius": 0.2 * mm});
            skCircle(sketch, "E612.MirrorC", {"center": v(-2.75, 6.6) * mm, "radius": 0.2 * mm});
            skCircle(sketch, "E613.MirrorC", {"center": v(-8.25, 1.1) * mm, "radius": 0.2 * mm});
            skCircle(sketch, "E614.MirrorC", {"center": v(-6.05, -2.2) * mm, "radius": 0.2 * mm});
            skCircle(sketch, "E615.MirrorC", {"center": v(-1.65, -3.85) * mm, "radius": 0.2 * mm});
            skCircle(sketch, "E616.MirrorC", {"center": v(-4.95, -8.25) * mm, "radius": 0.2 * mm});
            skCircle(sketch, "E617.MirrorC", {"center": v(-6.6, 6.6) * mm, "radius": 0.2 * mm});
            skCircle(sketch, "E618.MirrorC", {"center": v(-2.2, 1.65) * mm, "radius": 0.2 * mm});
            skCircle(sketch, "E619.MirrorC", {"center": v(-4.95, 3.3) * mm, "radius": 0.2 * mm});
            skCircle(sketch, "E620.MirrorC", {"center": v(-3.85, -7.7) * mm, "radius": 0.2 * mm});
            skCircle(sketch, "E621.MirrorC", {"center": v(-5.5, 5.5) * mm, "radius": 0.2 * mm});
            skCircle(sketch, "E622.MirrorC", {"center": v(-4.4, 4.4) * mm, "radius": 0.2 * mm});
            skCircle(sketch, "E623.MirrorC", {"center": v(-2.75, 8.25) * mm, "radius": 0.2 * mm});
            skCircle(sketch, "E624.MirrorC", {"center": v(-1.65, 2.75) * mm, "radius": 0.2 * mm});
            skCircle(sketch, "E625.MirrorC", {"center": v(-1.1, 3.85) * mm, "radius": 0.2 * mm});
            skCircle(sketch, "E626.MirrorC", {"center": v(-0.55, 5.5) * mm, "radius": 0.2 * mm});
            skCircle(sketch, "E627.MirrorC", {"center": v(-3.3, 3.85) * mm, "radius": 0.2 * mm});
            skCircle(sketch, "E628.MirrorC", {"center": v(-2.2, -6.05) * mm, "radius": 0.2 * mm});
            skCircle(sketch, "E629.MirrorC", {"center": v(-2.75, 1.1) * mm, "radius": 0.2 * mm});
            skCircle(sketch, "E630.MirrorC", {"center": v(-3.85, 4.95) * mm, "radius": 0.2 * mm});
            skCircle(sketch, "E631.MirrorC", {"center": v(-3.3, 8.25) * mm, "radius": 0.2 * mm});
            skCircle(sketch, "E632.MirrorC", {"center": v(-6.6, 4.4) * mm, "radius": 0.2 * mm});
            skCircle(sketch, "E633.MirrorC", {"center": v(-2.75, 9.35) * mm, "radius": 0.2 * mm});
            skCircle(sketch, "E634.MirrorC", {"center": v(-1.1, 8.25) * mm, "radius": 0.2 * mm});
            skCircle(sketch, "E635.MirrorC", {"center": v(-7.15, -1.65) * mm, "radius": 0.2 * mm});
            skCircle(sketch, "E636.MirrorC", {"center": v(-2.75, 0.55) * mm, "radius": 0.2 * mm});
            skCircle(sketch, "E637.MirrorC", {"center": v(-8.25, 2.75) * mm, "radius": 0.2 * mm});
            skCircle(sketch, "E638.MirrorC", {"center": v(-4.4, -8.25) * mm, "radius": 0.2 * mm});
            skCircle(sketch, "E639.MirrorC", {"center": v(-6.6, 3.3) * mm, "radius": 0.2 * mm});
            skCircle(sketch, "E640.MirrorC", {"center": v(-1.65, 6.6) * mm, "radius": 0.2 * mm});
            skCircle(sketch, "E641.MirrorC", {"center": v(-4.4, -3.3) * mm, "radius": 0.2 * mm});
            skCircle(sketch, "E642.MirrorC", {"center": v(-6.05, 6.6) * mm, "radius": 0.2 * mm});
            skCircle(sketch, "E643.MirrorC", {"center": v(-5.5, 6.6) * mm, "radius": 0.2 * mm});
            skCircle(sketch, "E644.MirrorC", {"center": v(-7.15, 5.5) * mm, "radius": 0.2 * mm});
            skCircle(sketch, "E645.MirrorC", {"center": v(-4.95, 6.6) * mm, "radius": 0.2 * mm});
            skCircle(sketch, "E646.MirrorC", {"center": v(-4.4, 7.15) * mm, "radius": 0.2 * mm});
            skCircle(sketch, "E647.MirrorC", {"center": v(-3.3, 8.8) * mm, "radius": 0.2 * mm});
            skCircle(sketch, "E648.MirrorC", {"center": v(-9.35, 1.1) * mm, "radius": 0.2 * mm});
            skCircle(sketch, "E649.MirrorC", {"center": v(-8.25, 3.3) * mm, "radius": 0.2 * mm});
            skCircle(sketch, "E650.MirrorC", {"center": v(-5.5, -1.65) * mm, "radius": 0.2 * mm});
            skCircle(sketch, "E651.MirrorC", {"center": v(-7.7, 1.1) * mm, "radius": 0.2 * mm});
            skCircle(sketch, "E652.MirrorC", {"center": v(-4.4, -8.8) * mm, "radius": 0.2 * mm});
            skCircle(sketch, "E653.MirrorC", {"center": v(-6.6, 7.15) * mm, "radius": 0.2 * mm});
            skCircle(sketch, "E654.MirrorC", {"center": v(-0.55, -2.75) * mm, "radius": 0.2 * mm});
            skCircle(sketch, "E655.MirrorC", {"center": v(-1.65, -7.15) * mm, "radius": 0.2 * mm});
            skCircle(sketch, "E656.MirrorC", {"center": v(-7.7, -3.85) * mm, "radius": 0.2 * mm});
            skCircle(sketch, "E657.MirrorC", {"center": v(-7.7, -0.55) * mm, "radius": 0.2 * mm});
            skCircle(sketch, "E658.MirrorC", {"center": v(-2.2, -0.55) * mm, "radius": 0.2 * mm});
            skCircle(sketch, "E659.MirrorC", {"center": v(-1.1, -4.4) * mm, "radius": 0.2 * mm});
            skCircle(sketch, "E660.MirrorC", {"center": v(-1.1, 8.8) * mm, "radius": 0.2 * mm});
            skCircle(sketch, "E661.MirrorC", {"center": v(-7.15, 3.3) * mm, "radius": 0.2 * mm});
            skCircle(sketch, "E662.MirrorC", {"center": v(-0.55, -8.8) * mm, "radius": 0.2 * mm});
            skCircle(sketch, "E663.MirrorC", {"center": v(-4.95, -2.75) * mm, "radius": 0.2 * mm});
            skCircle(sketch, "E664.MirrorC", {"center": v(-8.8, 3.85) * mm, "radius": 0.2 * mm});
            skCircle(sketch, "E665.MirrorC", {"center": v(-2.75, 5.5) * mm, "radius": 0.2 * mm});
            skCircle(sketch, "E666.MirrorC", {"center": v(-1.65, -4.95) * mm, "radius": 0.2 * mm});
            skCircle(sketch, "E667.MirrorC", {"center": v(-8.25, -4.4) * mm, "radius": 0.2 * mm});
            skCircle(sketch, "E668.MirrorC", {"center": v(-7.15, -1.1) * mm, "radius": 0.2 * mm});
            skCircle(sketch, "E669.MirrorC", {"center": v(-8.8, 2.2) * mm, "radius": 0.2 * mm});
            skCircle(sketch, "E670.MirrorC", {"center": v(-6.05, 6.05) * mm, "radius": 0.2 * mm});
            skCircle(sketch, "E671.MirrorC", {"center": v(-0.55, -5.5) * mm, "radius": 0.2 * mm});
            skCircle(sketch, "E672.MirrorC", {"center": v(-4.4, -5.5) * mm, "radius": 0.2 * mm});
            skCircle(sketch, "E673.MirrorC", {"center": v(-7.15, 4.95) * mm, "radius": 0.2 * mm});
            skCircle(sketch, "E674.MirrorC", {"center": v(-9.35, -2.2) * mm, "radius": 0.2 * mm});
            skCircle(sketch, "E675.MirrorC", {"center": v(-9.35, -2.75) * mm, "radius": 0.2 * mm});
            skCircle(sketch, "E676.MirrorC", {"center": v(-4.95, -1.65) * mm, "radius": 0.2 * mm});
            skCircle(sketch, "E677.MirrorC", {"center": v(-2.2, 6.05) * mm, "radius": 0.2 * mm});
            skCircle(sketch, "E678.MirrorC", {"center": v(-2.2, 5.5) * mm, "radius": 0.2 * mm});
            skCircle(sketch, "E679.MirrorC", {"center": v(-0.55, 9.9) * mm, "radius": 0.2 * mm});
            skCircle(sketch, "E680.MirrorC", {"center": v(-4.4, 2.75) * mm, "radius": 0.2 * mm});
            skCircle(sketch, "E681.MirrorC", {"center": v(-8.25, -2.2) * mm, "radius": 0.2 * mm});
            skCircle(sketch, "E682.MirrorC", {"center": v(-2.75, 4.95) * mm, "radius": 0.2 * mm});
            skCircle(sketch, "E683.MirrorC", {"center": v(-6.6, 2.75) * mm, "radius": 0.2 * mm});
            skCircle(sketch, "E684.MirrorC", {"center": v(-5.5, 2.2) * mm, "radius": 0.2 * mm});
            skCircle(sketch, "E685.MirrorC", {"center": v(-4.95, 2.2) * mm, "radius": 0.2 * mm});
            skCircle(sketch, "E686.MirrorC", {"center": v(-8.8, 1.65) * mm, "radius": 0.2 * mm});
            skCircle(sketch, "E687.MirrorC", {"center": v(-1.65, -8.25) * mm, "radius": 0.2 * mm});
            skCircle(sketch, "E688.MirrorC", {"center": v(-1.1, -4.95) * mm, "radius": 0.2 * mm});
            skCircle(sketch, "E689.MirrorC", {"center": v(-2.75, -8.25) * mm, "radius": 0.2 * mm});
            skCircle(sketch, "E690.MirrorC", {"center": v(-6.6, -5.5) * mm, "radius": 0.2 * mm});
            skCircle(sketch, "E691.MirrorC", {"center": v(-3.85, -2.75) * mm, "radius": 0.2 * mm});
            skCircle(sketch, "E692.MirrorC", {"center": v(-6.6, 5.5) * mm, "radius": 0.2 * mm});
            skCircle(sketch, "E693.MirrorC", {"center": v(-6.6, -2.2) * mm, "radius": 0.2 * mm});
            skCircle(sketch, "E694.MirrorC", {"center": v(-1.1, 9.35) * mm, "radius": 0.2 * mm});
            skCircle(sketch, "E695.MirrorC", {"center": v(-0.55, 3.3) * mm, "radius": 0.2 * mm});
            skCircle(sketch, "E696.MirrorC", {"center": v(-2.2, 8.25) * mm, "radius": 0.2 * mm});
            skCircle(sketch, "E697.MirrorC", {"center": v(-2.75, 8.8) * mm, "radius": 0.2 * mm});
            skCircle(sketch, "E698.MirrorC", {"center": v(-4.4, -1.65) * mm, "radius": 0.2 * mm});
            skCircle(sketch, "E699.MirrorC", {"center": v(-2.2, 8.8) * mm, "radius": 0.2 * mm});
            skCircle(sketch, "E700.MirrorC", {"center": v(-5.5, -1.1) * mm, "radius": 0.2 * mm});
            skCircle(sketch, "E701.MirrorC", {"center": v(-6.6, -1.65) * mm, "radius": 0.2 * mm});
            skCircle(sketch, "E702.MirrorC", {"center": v(-9.35, -0.55) * mm, "radius": 0.2 * mm});
            skCircle(sketch, "E703.MirrorC", {"center": v(-3.3, 6.6) * mm, "radius": 0.2 * mm});
            skCircle(sketch, "E704.MirrorC", {"center": v(-5.5, -3.3) * mm, "radius": 0.2 * mm});
            skCircle(sketch, "E705.MirrorC", {"center": v(-4.95, 5.5) * mm, "radius": 0.2 * mm});
            skCircle(sketch, "E706.MirrorC", {"center": v(-1.1, -3.85) * mm, "radius": 0.2 * mm});
            skCircle(sketch, "E707.MirrorC", {"center": v(-5.5, 6.05) * mm, "radius": 0.2 * mm});
            skCircle(sketch, "E708.MirrorC", {"center": v(-3.85, -6.05) * mm, "radius": 0.2 * mm});
            skCircle(sketch, "E709.MirrorC", {"center": v(-4.4, 2.2) * mm, "radius": 0.2 * mm});
            skCircle(sketch, "E710.MirrorC", {"center": v(-3.85, -4.95) * mm, "radius": 0.2 * mm});
            skCircle(sketch, "E711.MirrorC", {"center": v(-0.55, 1.65) * mm, "radius": 0.2 * mm});
            skCircle(sketch, "E712.MirrorC", {"center": v(-8.25, -4.95) * mm, "radius": 0.2 * mm});
            skCircle(sketch, "E713.MirrorC", {"center": v(-1.65, 7.7) * mm, "radius": 0.2 * mm});
            skCircle(sketch, "E714.MirrorC", {"center": v(-7.7, 4.4) * mm, "radius": 0.2 * mm});
            skCircle(sketch, "E715.MirrorC", {"center": v(-4.4, 3.3) * mm, "radius": 0.2 * mm});
            skCircle(sketch, "E716.MirrorC", {"center": v(-2.75, -0.55) * mm, "radius": 0.2 * mm});
            skCircle(sketch, "E717.MirrorC", {"center": v(-3.85, 3.85) * mm, "radius": 0.2 * mm});
            skCircle(sketch, "E718.MirrorC", {"center": v(-6.05, 7.15) * mm, "radius": 0.2 * mm});
            skCircle(sketch, "E719.MirrorC", {"center": v(-7.7, 5.5) * mm, "radius": 0.2 * mm});
            skCircle(sketch, "E720.MirrorC", {"center": v(-4.95, 2.75) * mm, "radius": 0.2 * mm});
            skCircle(sketch, "E721.MirrorC", {"center": v(-3.3, -1.1) * mm, "radius": 0.2 * mm});
            skCircle(sketch, "E722.MirrorC", {"center": v(-7.7, 6.05) * mm, "radius": 0.2 * mm});
            skCircle(sketch, "E723.MirrorC", {"center": v(-3.3, -7.15) * mm, "radius": 0.2 * mm});
            skCircle(sketch, "E724.MirrorC", {"center": v(-4.95, -2.2) * mm, "radius": 0.2 * mm});
            skCircle(sketch, "E725.MirrorC", {"center": v(-1.65, -3.3) * mm, "radius": 0.2 * mm});
            skCircle(sketch, "E726.MirrorC", {"center": v(-5.5, 3.3) * mm, "radius": 0.2 * mm});
            skCircle(sketch, "E727.MirrorC", {"center": v(-9.9, 0) * mm, "radius": 0.2 * mm});
            skCircle(sketch, "E728.MirrorC", {"center": v(-0.55, -3.3) * mm, "radius": 0.2 * mm});
            skCircle(sketch, "E729.MirrorC", {"center": v(-3.3, 1.1) * mm, "radius": 0.2 * mm});
            skCircle(sketch, "E730.MirrorC", {"center": v(-2.2, -4.95) * mm, "radius": 0.2 * mm});
            skCircle(sketch, "E731.MirrorC", {"center": v(-1.1, -1.65) * mm, "radius": 0.2 * mm});
            skCircle(sketch, "E732.MirrorC", {"center": v(-1.65, -2.75) * mm, "radius": 0.2 * mm});
            skCircle(sketch, "E733.MirrorC", {"center": v(-6.6, -4.4) * mm, "radius": 0.2 * mm});
            skCircle(sketch, "E734.MirrorC", {"center": v(-6.6, -0.55) * mm, "radius": 0.2 * mm});
            skCircle(sketch, "E735.MirrorC", {"center": v(-1.65, -1.1) * mm, "radius": 0.2 * mm});
            skCircle(sketch, "E736.MirrorC", {"center": v(-6.05, 4.4) * mm, "radius": 0.2 * mm});
            skCircle(sketch, "E737.MirrorC", {"center": v(-5.5, 3.85) * mm, "radius": 0.2 * mm});
            skCircle(sketch, "E738.MirrorC", {"center": v(-6.05, -6.6) * mm, "radius": 0.2 * mm});
            skCircle(sketch, "E739.MirrorC", {"center": v(-6.05, -1.65) * mm, "radius": 0.2 * mm});
            skCircle(sketch, "E740.MirrorC", {"center": v(-1.65, 7.15) * mm, "radius": 0.2 * mm});
            skCircle(sketch, "E741.MirrorC", {"center": v(-6.6, -3.85) * mm, "radius": 0.2 * mm});
            skCircle(sketch, "E742.MirrorC", {"center": v(-3.85, -2.2) * mm, "radius": 0.2 * mm});
            skCircle(sketch, "E743.MirrorC", {"center": v(-9.9, -0.55) * mm, "radius": 0.2 * mm});
            skCircle(sketch, "E744.MirrorC", {"center": v(-1.1, -2.75) * mm, "radius": 0.2 * mm});
            skCircle(sketch, "E745.MirrorC", {"center": v(-1.1, 0.55) * mm, "radius": 0.2 * mm});
            skCircle(sketch, "E746.MirrorC", {"center": v(-8.8, -2.75) * mm, "radius": 0.2 * mm});
            skCircle(sketch, "E747.MirrorC", {"center": v(-3.3, 4.95) * mm, "radius": 0.2 * mm});
            skCircle(sketch, "E748.MirrorC", {"center": v(-4.95, -7.7) * mm, "radius": 0.2 * mm});
            skCircle(sketch, "E749.MirrorC", {"center": v(-2.75, -4.4) * mm, "radius": 0.2 * mm});
            skCircle(sketch, "E750.MirrorC", {"center": v(-2.75, 6.05) * mm, "radius": 0.2 * mm});
            skCircle(sketch, "E751.MirrorC", {"center": v(-5.5, -4.4) * mm, "radius": 0.2 * mm});
            skCircle(sketch, "E752.MirrorC", {"center": v(-4.95, -6.05) * mm, "radius": 0.2 * mm});
            skCircle(sketch, "E753.MirrorC", {"center": v(-1.65, 8.25) * mm, "radius": 0.2 * mm});
            skCircle(sketch, "E754.MirrorC", {"center": v(-4.95, 3.85) * mm, "radius": 0.2 * mm});
            skCircle(sketch, "E755.MirrorC", {"center": v(-4.4, 6.05) * mm, "radius": 0.2 * mm});
            skCircle(sketch, "E756.MirrorC", {"center": v(-0.55, 1.1) * mm, "radius": 0.2 * mm});
            skCircle(sketch, "E757", {"center": v(0, 0) * mm, "radius": 40 * mm});
            skSolve(sketch);
        }
        {
            var Q0;
            Q0=makeQuery(id+"F0.imprint","IMPRINT",FACE,{"disambiguationData":[TD([[makeQuery(id+"F0.imprint","IMPRINT",EDGE,{"derivedFrom":sQuery(id+"F0.wireOp",EDGE,"E0")}),-1.0]])]});
            extrude(context, id + "F1", {"entities" : qUnion([Q0]), "depth" : 0.5 * mm});
        }
    });
